FCSTD DOCUMENT  (FreeCAD 0.19R24344 (Git))
Label: MicroManipulator_Assembly_Figure2
Comment: The assembled MicroManipulator. This assembly consists of six parts. The type of arm depends on the application, the one currently shown is intended for the tethering station.
License: Creative Commons Attribution-NonCommercial-ShareAlike
LicenseURL: http://creativecommons.org/licenses/by-nc-sa/4.0/
objects: Part::FeaturePython×30, App::Link×15, App::DocumentObjectGroup×2, PartDesign::CoordinateSystem×1, App::FeaturePython×1, App::Part×1
note: 31 computed .brp shape members not serialized (recipe doc carries the construction recipe); baked Part::Feature solids carry a one-line shape summary decoded from their .brp
EXTERNAL_REF file=MicroManipulator_Rail_bottom.FCStd obj=Bottom_Mount_Edge
EXTERNAL_REF file=MicroManipulator_Rail_bottom.FCStd obj=Body
EXTERNAL_REF file=MicroManipulator_Carriage_bottom-center.FCStd obj=ScrewBottom_LCS
EXTERNAL_REF file=MicroManipulator_Rail_bottom.FCStd obj=Bottom_Cage_LCS
EXTERNAL_REF file=MicroManipulator_Carriage_bottom-center.FCStd obj=CenterSlider
EXTERNAL_REF file=MicroManipulator_Carriage_bottom-center.FCStd obj=ScrewTop_LCS
EXTERNAL_REF file=MicroManipulator_Rail_center.FCStd obj=Screw_LCS
EXTERNAL_REF file=MicroManipulator_Rail_center.FCStd obj=CenterCage
EXTERNAL_REF file=MicroManipulator_Rail_center.FCStd obj=Top_Mount_LCS
EXTERNAL_REF file=MicroManipulator_Rail_top.FCStd obj=MountPoint_LCS
EXTERNAL_REF file=MicroManipulator_Rail_top.FCStd obj=CageTop
EXTERNAL_REF file=MicroManipulator_Carriage_Hinge_top.FCStd obj=Screw_LCS
EXTERNAL_REF file=MicroManipulator_Rail_top.FCStd obj=Screw_LCS
EXTERNAL_REF file=MicroManipulator_Carriage_Hinge_top.FCStd obj=Slider
EXTERNAL_REF file=MicroManipulator_Arm_TetherStation.FCStd obj=ArmMount_LCS
EXTERNAL_REF file=MicroManipulator_Carriage_Hinge_top.FCStd obj=ArmMount_LCS
EXTERNAL_REF file=MicroManipulator_Arm_TetherStation.FCStd obj=TetherArm
EXTERNAL_REF file=MicroManipulator_Arm_tilted_Arena.FCStd obj=LCS_Hinge
EXTERNAL_REF file=MicroManipulator_Arm_tilted_Arena.FCStd obj=Body
EXTERNAL_REF file=MicroManipulator_Arm_tilted_Arena.FCStd obj=LCS_Luer
EXTERNAL_REF file=../../Miscellaneous/Luer-Tether/Luer-Tether.FCStd obj=Part
EXTERNAL_REF file=MicroManipulator_Rail_top.FCStd obj=LCS_Fasten_1
EXTERNAL_REF file=MicroManipulator_Rail_top.FCStd obj=LCS_Fasten_2
EXTERNAL_REF file=MicroManipulator_Rail_top.FCStd obj=LCS_Fasten_3
EXTERNAL_REF file=MicroManipulator_Rail_top.FCStd obj=LCS_Fasten_4
EXTERNAL_REF file=MicroManipulator_Handle.FCStd obj=LCS_Handle
EXTERNAL_REF file=MicroManipulator_Handle.FCStd obj=Body
EXTERNAL_REF file=MicroManipulator_Rail_bottom.FCStd obj=LCS_Fasten_1
EXTERNAL_REF file=MicroManipulator_Rail_bottom.FCStd obj=LCS_Fasten_2
EXTERNAL_REF file=MicroManipulator_Rail_bottom.FCStd obj=LCS_Fasten_3
EXTERNAL_REF file=MicroManipulator_Rail_bottom.FCStd obj=LCS_Fasten_4
EXTERNAL_REF file=../../Miscellaneous/Scale-Bar/Scale-Bar.FCStd obj=Scalebar

FEATURE [App::DocumentObjectGroup] Parts
FEATURE [PartDesign::CoordinateSystem] LCS_Origin
  AttacherType = Attacher::AttachEngine3D
  MapMode = 2
  Support = -> [X_Axis]
FEATURE [App::DocumentObjectGroup] Constraints
FEATURE [App::FeaturePython] Variables  # WARN: FeaturePython — macro-defined, semantics opaque (R4)
  ArmRotation = 0
  BottomMovement = 8.3
  CenterMovement = 14
  TopMovement = 5
FEATURE [App::Link] Micro_Cage_bottom
FEATURE [App::Link] Micro_Cage_bottom001
FEATURE [App::Link] Micro_Cage_bottom_Body
  AssemblyType = Asm4EE
  AttachedBy = #Bottom_Mount_Edge
  AttachedTo = Parent Assembly#LCS_Origin
  LinkPlacement = pos=(-12.7,32.4,4) rot=(0,0,-1;1.5708rad)
  LinkedObject = -> <external MicroManipulator_Rail_bottom.FCStd>#Body
  Placement = pos=(-12.7,32.4,4) rot=(0,0,-1;1.5708rad)
  expr: Placement = LCS_Origin.Placement * AttachmentOffset * MicroManipulator_Rail_bottom#Bottom_Mount_Edge.Placement ^ -1
FEATURE [App::Link] CenterSliderCombined_CenterSlider
  AssemblyType = Asm4EE
  AttachedBy = #ScrewBottom_LCS
  AttachedTo = Micro_Cage_bottom_Body#Bottom_Cage_LCS
  AttachmentOffset = pos=(0,0,8.3) rot=(0,0,1;0rad)
  LinkPlacement = pos=(-12.7,24.1,4) rot=(0,0,-1;1.5708rad)
  LinkedObject = -> <external MicroManipulator_Carriage_bottom-center.FCStd>#CenterSlider
  Placement = pos=(-12.7,24.1,4) rot=(0,0,-1;1.5708rad)
  expr: .AttachmentOffset.Base.z = Variables.BottomMovement
  expr: Placement = Micro_Cage_bottom_Body.Placement * MicroManipulator_Rail_bottom#Bottom_Cage_LCS.Placement * AttachmentOffset * MicroManipulator_Carriage_bottom_center#ScrewBottom_LCS.Placement ^ -1
FEATURE [App::Link] CenterCage
  AssemblyType = Asm4EE
  AttachedBy = #Screw_LCS
  AttachedTo = CenterSliderCombined_CenterSlider#ScrewTop_LCS
  AttachmentOffset = pos=(0,0,14) rot=(0,1,0;3.14159rad)
  LinkPlacement = pos=(-36.7,12.1,23) rot=(1,0,0;3.14159rad)
  LinkedObject = -> <external MicroManipulator_Rail_center.FCStd>#CenterCage
  Placement = pos=(-36.7,12.1,23) rot=(1,0,0;3.14159rad)
  expr: .AttachmentOffset.Base.z = Variables.CenterMovement
  expr: Placement = CenterSliderCombined_CenterSlider.Placement * MicroManipulator_Carriage_bottom_center#ScrewTop_LCS.Placement * AttachmentOffset * MicroManipulator_Rail_center#Screw_LCS.Placement ^ -1
FEATURE [App::Link] CageTop
  AssemblyType = Asm4EE
  AttachedBy = #MountPoint_LCS
  AttachedTo = CenterCage#Top_Mount_LCS
  AttachmentOffset = pos=(0,0,0) rot=(0,0,1;3.14159rad)
  LinkPlacement = pos=(-20.7,12.1,66) rot=(-3e-06,-1,2e-06;4.71239rad)
  LinkedObject = -> <external MicroManipulator_Rail_top.FCStd>#CageTop
  Placement = pos=(-20.7,12.1,66) rot=(-3e-06,-1,2e-06;4.71239rad)
  expr: Placement = CenterCage.Placement * MicroManipulator_Rail_center#Top_Mount_LCS.Placement * AttachmentOffset * MicroManipulator_Rail_top#MountPoint_LCS.Placement ^ -1
FEATURE [App::Link] SliderTop
  AssemblyType = Asm4EE
  AttachedBy = #Screw_LCS
  AttachedTo = CageTop#Screw_LCS
  AttachmentOffset = pos=(0,0,5) rot=(0,0,1;0rad)
  LinkPlacement = pos=(-20.7,12.1,63) rot=(-3e-06,-1,2e-06;4.71239rad)
  LinkedObject = -> <external MicroManipulator_Carriage_Hinge_top.FCStd>#Slider
  Placement = pos=(-20.7,12.1,63) rot=(-3e-06,-1,2e-06;4.71239rad)
  expr: .AttachmentOffset.Base.z = Variables.TopMovement
  expr: Placement = CageTop.Placement * MicroManipulator_Rail_top#Screw_LCS.Placement * AttachmentOffset * MicroManipulator_Carriage_Hinge_top#Screw_LCS.Placement ^ -1
FEATURE [App::Link] TetherArm
  AssemblyType = Asm4EE
  AttachedBy = #ArmMount_LCS
  AttachedTo = SliderTop#ArmMount_LCS
  AttachmentOffset = pos=(12,6,26) rot=(0,0,1;-0.523599rad)
  LinkPlacement = pos=(2.29989,0.0999279,76.5) rot=(0,0,1;2.61799rad)
  LinkedObject = -> <external MicroManipulator_Arm_TetherStation.FCStd>#TetherArm
  Placement = pos=(2.29989,0.0999279,76.5) rot=(0,0,1;2.61799rad)
  expr: Placement = SliderTop.Placement * MicroManipulator_Carriage_Hinge_top#ArmMount_LCS.Placement * AttachmentOffset * MicroManipulator_Arm_TetherStation#ArmMount_LCS.Placement ^ -1
FEATURE [Part::FeaturePython] Screw  # WARN: FeaturePython — macro-defined, semantics opaque (R4)
  invert = false
  offset = 0
FEATURE [Part::FeaturePython] Screw001  # WARN: FeaturePython — macro-defined, semantics opaque (R4)
  invert = false
  offset = 0
FEATURE [App::Link] MicroManipulator_Arm_tilted_Arena_Arm_tilted_Arena
  AssemblyType = Asm4EE
  AttachedBy = #LCS_Hinge
  AttachedTo = SliderTop#ArmMount_LCS
  AttachmentOffset = pos=(0,0,0) rot=(0,0,1;-0.471239rad)
  LinkPlacement = pos=(-3.70005,12.1,50.5) rot=(0,0,1;2.67035rad)
  LinkedObject = -> <external MicroManipulator_Arm_tilted_Arena.FCStd>#Body
  Placement = pos=(-3.70005,12.1,50.5) rot=(0,0,1;2.67035rad)
  expr: Placement = SliderTop.Placement * MicroManipulator_Carriage_Hinge_top#ArmMount_LCS.Placement * AttachmentOffset * MicroManipulator_Arm_tilted_Arena#LCS_Hinge.Placement ^ -1
FEATURE [App::Link] Luer_Tether_Part
  AssemblyType = Asm4EE
  AttachedBy = #LCS_Luer
  AttachedTo = MicroManipulator_Arm_tilted_Arena_Arm_tilted_Arena#LCS_Luer
  AttachmentOffset = pos=(0,0,6) rot=(0,0,1;0rad)
  LinkPlacement = pos=(52.5794,-20.6202,50.0652) rot=(0.443537,-0.72379,0.528586;1.71809rad)
  LinkedObject = -> <external ../../Miscellaneous/Luer-Tether/Luer-Tether.FCStd>#Part
  Placement = pos=(52.5794,-20.6202,50.0652) rot=(0.443537,-0.72379,0.528586;1.71809rad)
  expr: Placement = MicroManipulator_Arm_tilted_Arena_Arm_tilted_Arena.Placement * MicroManipulator_Arm_tilted_Arena#LCS_Luer.Placement * AttachmentOffset * Luer_Tether#LCS_Luer.Placement ^ -1
FEATURE [Part::FeaturePython] Washer  label="M3-Washer"  # Fasteners workbench fastener (typed FeaturePython)
  AssemblyType = Asm4EE
  AttachedBy = Origin
  AttachedTo = CageTop#Screw_LCS
  AttachmentOffset = pos=(0,0,0) rot=(1,0,0;3.14159rad)
  Placement = pos=(-15.7,12.1,68) rot=(0,0,1;1.57079rad)
  diameter = 4
  invert = false
  matchOuter = false
  offset = 0
  type = 3
  expr: Placement = CageTop.Placement * MicroManipulator_Rail_top#Screw_LCS.Placement * AttachmentOffset
FEATURE [Part::FeaturePython] Washer001  label="M3-Washer035"  # Fasteners workbench fastener (typed FeaturePython)
  AssemblyType = Asm4EE
  AttachedBy = Origin
  AttachedTo = CageTop#Screw_LCS
  AttachmentOffset = pos=(0,0,2.7) rot=(1,0,0;3.14159rad)
  Placement = pos=(-15.7,12.1,65.3) rot=(0,0,1;1.57079rad)
  diameter = 4
  invert = false
  matchOuter = false
  offset = 0
  type = 3
  expr: Placement = CageTop.Placement * MicroManipulator_Rail_top#Screw_LCS.Placement * AttachmentOffset
FEATURE [Part::FeaturePython] Screw002  label="M3x40-Screw"  # Fasteners workbench fastener (typed FeaturePython)
  AssemblyType = Asm4EE
  AttachedBy = Origin
  AttachedTo = CageTop#Screw_LCS
  AttachmentOffset = pos=(0,0,-0.5) rot=(1,0,0;3.14159rad)
  Placement = pos=(-15.7,12.1,68.5) rot=(0,0,1;1.57079rad)
  diameter = 4
  invert = false
  length = 10
  lengthCustom = 40
  matchOuter = false
  offset = 0
  thread = true
  type = 27
  expr: Placement = CageTop.Placement * MicroManipulator_Rail_top#Screw_LCS.Placement * AttachmentOffset
FEATURE [Part::FeaturePython] Nut  label="M3-Nut075"  # Fasteners workbench fastener (typed FeaturePython)
  AssemblyType = Asm4EE
  AttachedBy = Origin
  AttachedTo = CageTop#Screw_LCS
  AttachmentOffset = pos=(0,0,2.8) rot=(0,0,1;0rad)
  Placement = pos=(-15.7,12.1,65.2) rot=(0.707109,0.707105,0;3.14159rad)
  diameter = 4
  invert = false
  matchOuter = false
  offset = 0
  thread = false
  type = 7
  expr: Placement = CageTop.Placement * MicroManipulator_Rail_top#Screw_LCS.Placement * AttachmentOffset
FEATURE [Part::FeaturePython] Nut001  label="M3-Nut076"  # Fasteners workbench fastener (typed FeaturePython)
  AssemblyType = Asm4EE
  AttachedBy = Origin
  AttachedTo = SliderTop#ArmMount_LCS
  AttachmentOffset = pos=(0,0,-5) rot=(0,0,1;0rad)
  Placement = pos=(-3.70005,12.1,45.5) rot=(0,0,-1;1.5708rad)
  diameter = 4
  invert = false
  matchOuter = false
  offset = 0
  thread = false
  type = 7
  expr: Placement = SliderTop.Placement * MicroManipulator_Carriage_Hinge_top#ArmMount_LCS.Placement * AttachmentOffset
FEATURE [Part::FeaturePython] Screw003  label="M3x10-Screw"  # Fasteners workbench fastener (typed FeaturePython)
  AssemblyType = Asm4EE
  AttachedBy = Origin
  AttachedTo = SliderTop#ArmMount_LCS
  AttachmentOffset = pos=(0,0,4.4) rot=(0,0,1;0rad)
  Placement = pos=(-3.70005,12.1,54.9) rot=(0,0,-1;1.5708rad)
  diameter = 4
  invert = false
  length = 3
  lengthCustom = 10
  matchOuter = false
  offset = 0
  thread = false
  type = 27
  expr: Placement = SliderTop.Placement * MicroManipulator_Carriage_Hinge_top#ArmMount_LCS.Placement * AttachmentOffset
FEATURE [Part::FeaturePython] Screw004  label="M3x6-Screw"  # Fasteners workbench fastener (typed FeaturePython)
  AssemblyType = Asm4EE
  AttachedBy = Origin
  AttachedTo = CageTop#LCS_Fasten_1
  AttachmentOffset = pos=(0,0,0) rot=(1,0,0;3.14159rad)
  Placement = pos=(-11.7001,2.1,28) rot=(0.009203,0.012998,-0.999873;5e-06rad)
  diameter = 4
  invert = false
  length = 1
  lengthCustom = 6
  matchOuter = false
  offset = 0
  thread = false
  type = 27
  expr: Placement = CageTop.Placement * MicroManipulator_Rail_top#LCS_Fasten_1.Placement * AttachmentOffset
FEATURE [Part::FeaturePython] Screw005  label="M3x6-Screw028"  # Fasteners workbench fastener (typed FeaturePython)
  AssemblyType = Asm4EE
  AttachedBy = Origin
  AttachedTo = CageTop#LCS_Fasten_2
  AttachmentOffset = pos=(0,0,0) rot=(0,-1,0;3.14159rad)
  Placement = pos=(-21.7001,2.10005,28) rot=(0,0,1;3.14159rad)
  diameter = 4
  invert = false
  length = 1
  lengthCustom = 6
  matchOuter = false
  offset = 0
  thread = false
  type = 27
  expr: Placement = CageTop.Placement * MicroManipulator_Rail_top#LCS_Fasten_2.Placement * AttachmentOffset
FEATURE [Part::FeaturePython] Screw006  label="M3x6-Screw029"  # Fasteners workbench fastener (typed FeaturePython)
  AssemblyType = Asm4EE
  AttachedBy = Origin
  AttachedTo = CageTop#LCS_Fasten_3
  AttachmentOffset = pos=(0,0,0) rot=(1,0,0;3.14159rad)
  Placement = pos=(-11.7,22.1,28) rot=(0.009203,0.012998,-0.999873;5e-06rad)
  diameter = 4
  invert = false
  length = 1
  lengthCustom = 6
  matchOuter = false
  offset = 0
  thread = false
  type = 27
  expr: Placement = CageTop.Placement * MicroManipulator_Rail_top#LCS_Fasten_3.Placement * AttachmentOffset
FEATURE [Part::FeaturePython] Screw007  label="M3x6-Screw030"  # Fasteners workbench fastener (typed FeaturePython)
  AssemblyType = Asm4EE
  AttachedBy = Origin
  AttachedTo = CageTop#LCS_Fasten_4
  AttachmentOffset = pos=(0,0,0) rot=(1,0,0;3.14159rad)
  Placement = pos=(-21.7,22.1,28) rot=(0.009203,0.012998,-0.999873;5e-06rad)
  diameter = 4
  invert = false
  length = 1
  lengthCustom = 6
  matchOuter = false
  offset = 0
  thread = false
  type = 27
  expr: Placement = CageTop.Placement * MicroManipulator_Rail_top#LCS_Fasten_4.Placement * AttachmentOffset
FEATURE [Part::FeaturePython] Nut002  label="M3-Nut"  # Fasteners workbench fastener (typed FeaturePython)
  AssemblyType = Asm4EE
  AttachedBy = Origin
  AttachedTo = SliderTop#Screw_LCS
  AttachmentOffset = pos=(0,0,4.5) rot=(0,0,-1;1.5708rad)
  Placement = pos=(-15.7,12.1,58.5) rot=(2e-06,1,0;3.14159rad)
  diameter = 4
  invert = false
  matchOuter = false
  offset = 0
  thread = false
  type = 7
  expr: Placement = SliderTop.Placement * MicroManipulator_Carriage_Hinge_top#Screw_LCS.Placement * AttachmentOffset
FEATURE [Part::FeaturePython] Nut003  label="M3-Nut077"  # Fasteners workbench fastener (typed FeaturePython)
  AssemblyType = Asm4EE
  AttachedBy = Origin
  AttachedTo = CageTop#LCS_Fasten_1
  AttachmentOffset = pos=(0,0,4) rot=(0,0,-1;3.14159rad)
  Placement = pos=(-11.7001,2.1,24) rot=(3e-06,1,0;3.14159rad)
  diameter = 4
  invert = false
  matchOuter = false
  offset = 0
  thread = false
  type = 7
  expr: Placement = CageTop.Placement * MicroManipulator_Rail_top#LCS_Fasten_1.Placement * AttachmentOffset
FEATURE [Part::FeaturePython] Nut004  label="M3-Nut078"  # Fasteners workbench fastener (typed FeaturePython)
  AssemblyType = Asm4EE
  AttachedBy = Origin
  AttachedTo = CageTop#LCS_Fasten_2
  AttachmentOffset = pos=(0,0,4) rot=(0,0,1;0rad)
  Placement = pos=(-21.7001,2.10005,24) rot=(1,-3e-06,0;3.14159rad)
  diameter = 4
  invert = false
  matchOuter = false
  offset = 0
  thread = false
  type = 7
  expr: Placement = CageTop.Placement * MicroManipulator_Rail_top#LCS_Fasten_2.Placement * AttachmentOffset
FEATURE [Part::FeaturePython] Nut005  label="M3-Nut079"  # Fasteners workbench fastener (typed FeaturePython)
  AssemblyType = Asm4EE
  AttachedBy = Origin
  AttachedTo = CageTop#LCS_Fasten_3
  AttachmentOffset = pos=(0,0,4) rot=(0,0,1;0rad)
  Placement = pos=(-11.7,22.1,24) rot=(1,-3e-06,0;3.14159rad)
  diameter = 4
  invert = false
  matchOuter = false
  offset = 0
  thread = false
  type = 7
  expr: Placement = CageTop.Placement * MicroManipulator_Rail_top#LCS_Fasten_3.Placement * AttachmentOffset
FEATURE [Part::FeaturePython] Nut006  label="M3-Nut080"  # Fasteners workbench fastener (typed FeaturePython)
  AssemblyType = Asm4EE
  AttachedBy = Origin
  AttachedTo = CageTop#LCS_Fasten_4
  AttachmentOffset = pos=(0,0,4) rot=(0,0,1;0rad)
  Placement = pos=(-21.7,22.1,24) rot=(1,-3e-06,0;3.14159rad)
  diameter = 4
  invert = false
  matchOuter = false
  offset = 0
  thread = false
  type = 7
  expr: Placement = CageTop.Placement * MicroManipulator_Rail_top#LCS_Fasten_4.Placement * AttachmentOffset
FEATURE [Part::FeaturePython] Screw008  label="M3x40-Screw007"  # Fasteners workbench fastener (typed FeaturePython)
  AssemblyType = Asm4EE
  AttachedBy = Origin
  AttachedTo = CenterCage#Screw_LCS
  AttachmentOffset = pos=(0,0,-0.7) rot=(1,0,0;3.14159rad)
  Placement = pos=(-39.4,12.1,18) rot=(0.57735,-0.57735,-0.57735;2.0944rad)
  diameter = 4
  invert = false
  length = 10
  lengthCustom = 40
  matchOuter = false
  offset = 0
  thread = true
  type = 27
  expr: Placement = CenterCage.Placement * MicroManipulator_Rail_center#Screw_LCS.Placement * AttachmentOffset
FEATURE [Part::FeaturePython] Washer002  label="M3-Washer033"  # Fasteners workbench fastener (typed FeaturePython)
  AssemblyType = Asm4EE
  AttachedBy = Origin
  AttachedTo = CenterCage#Screw_LCS
  AttachmentOffset = pos=(0,0,0) rot=(1,0,0;3.14159rad)
  Placement = pos=(-38.7,12.1,18) rot=(0.57735,-0.57735,-0.57735;2.0944rad)
  diameter = 4
  invert = false
  matchOuter = false
  offset = 0
  type = 3
  expr: Placement = CenterCage.Placement * MicroManipulator_Rail_center#Screw_LCS.Placement * AttachmentOffset
FEATURE [Part::FeaturePython] Washer003  label="M3-Washer034"  # Fasteners workbench fastener (typed FeaturePython)
  AssemblyType = Asm4EE
  AttachedBy = Origin
  AttachedTo = CenterCage#Screw_LCS
  AttachmentOffset = pos=(0,0,2) rot=(0,0,1;0rad)
  Placement = pos=(-36.7,12.1,18) rot=(0.57735,-0.57735,0.57735;4.18879rad)
  diameter = 4
  invert = false
  matchOuter = false
  offset = 0
  type = 3
  expr: Placement = CenterCage.Placement * MicroManipulator_Rail_center#Screw_LCS.Placement * AttachmentOffset
FEATURE [Part::FeaturePython] Nut007  label="M3-Nut081"  # Fasteners workbench fastener (typed FeaturePython)
  AssemblyType = Asm4EE
  AttachedBy = Origin
  AttachedTo = CenterCage#Screw_LCS
  AttachmentOffset = pos=(0,0,2.8) rot=(0,0,1;0rad)
  Placement = pos=(-35.9,12.1,18) rot=(0.57735,-0.57735,0.57735;4.18879rad)
  diameter = 4
  invert = false
  matchOuter = false
  offset = 0
  thread = false
  type = 7
  expr: Placement = CenterCage.Placement * MicroManipulator_Rail_center#Screw_LCS.Placement * AttachmentOffset
FEATURE [Part::FeaturePython] Screw009  label="M3x40-Screw006"  # Fasteners workbench fastener (typed FeaturePython)
  AssemblyType = Asm4EE
  AttachedBy = Origin
  AttachedTo = Micro_Cage_bottom_Body#Bottom_Cage_LCS
  AttachmentOffset = pos=(0,0,-0.7) rot=(1,0,0;3.14159rad)
  Placement = pos=(-12.7,33.1,9) rot=(-1,0,0;1.5708rad)
  diameter = 4
  invert = false
  length = 10
  lengthCustom = 40
  matchOuter = false
  offset = 0
  thread = true
  type = 27
  expr: Placement = Micro_Cage_bottom_Body.Placement * MicroManipulator_Rail_bottom#Bottom_Cage_LCS.Placement * AttachmentOffset
FEATURE [Part::FeaturePython] Washer004  label="M3-Washer028"  # Fasteners workbench fastener (typed FeaturePython)
  AssemblyType = Asm4EE
  AttachedBy = Origin
  AttachedTo = Micro_Cage_bottom_Body#Bottom_Cage_LCS
  AttachmentOffset = pos=(0,0,0) rot=(1,0,0;3.14159rad)
  Placement = pos=(-12.7,32.4,9) rot=(-1,0,0;1.5708rad)
  diameter = 4
  invert = false
  matchOuter = false
  offset = 0
  type = 3
  expr: Placement = Micro_Cage_bottom_Body.Placement * MicroManipulator_Rail_bottom#Bottom_Cage_LCS.Placement * AttachmentOffset
FEATURE [Part::FeaturePython] Washer005  label="M3-Washer029"  # Fasteners workbench fastener (typed FeaturePython)
  AssemblyType = Asm4EE
  AttachedBy = Origin
  AttachedTo = Micro_Cage_bottom_Body#Bottom_Cage_LCS
  AttachmentOffset = pos=(0,0,2) rot=(0,0,1;0rad)
  Placement = pos=(-12.7,30.4,9) rot=(1,0,0;1.5708rad)
  diameter = 4
  invert = false
  matchOuter = false
  offset = 0
  type = 3
  expr: Placement = Micro_Cage_bottom_Body.Placement * MicroManipulator_Rail_bottom#Bottom_Cage_LCS.Placement * AttachmentOffset
FEATURE [Part::FeaturePython] Nut008  label="M3-Nut064"  # Fasteners workbench fastener (typed FeaturePython)
  AssemblyType = Asm4EE
  AttachedBy = Origin
  AttachedTo = Micro_Cage_bottom_Body#Bottom_Cage_LCS
  AttachmentOffset = pos=(0,0,2.7) rot=(0,0,1;0rad)
  Placement = pos=(-12.7,29.7,9) rot=(1,0,0;1.5708rad)
  diameter = 4
  invert = false
  matchOuter = false
  offset = 0
  thread = false
  type = 7
  expr: Placement = Micro_Cage_bottom_Body.Placement * MicroManipulator_Rail_bottom#Bottom_Cage_LCS.Placement * AttachmentOffset
FEATURE [Part::FeaturePython] Nut009  label="M3-Nut082"  # Fasteners workbench fastener (typed FeaturePython)
  AssemblyType = Asm4EE
  AttachedBy = Origin
  AttachedTo = CageTop#Screw_LCS
  AttachmentOffset = pos=(0,0,22) rot=(0,0,1;0rad)
  Placement = pos=(-15.7,12.1,46) rot=(0.707109,0.707105,0;3.14159rad)
  diameter = 4
  invert = false
  matchOuter = false
  offset = 0
  thread = false
  type = 7
  expr: Placement = CageTop.Placement * MicroManipulator_Rail_top#Screw_LCS.Placement * AttachmentOffset
FEATURE [App::Link] MicroManipulator_Handle_Handle
  AssemblyType = Asm4EE
  AttachedBy = #LCS_Handle
  AttachedTo = Micro_Cage_bottom_Body#Bottom_Cage_LCS
  AttachmentOffset = pos=(0,0,-1) rot=(1,0,0;3.14159rad)
  LinkPlacement = pos=(-12.7,33.4,9) rot=(0.935113,0.250563,0.250563;4.64535rad)
  LinkedObject = -> <external MicroManipulator_Handle.FCStd>#Body
  Placement = pos=(-12.7,33.4,9) rot=(0.935113,0.250563,0.250563;4.64535rad)
  expr: Placement = Micro_Cage_bottom_Body.Placement * MicroManipulator_Rail_bottom#Bottom_Cage_LCS.Placement * AttachmentOffset * MicroManipulator_Handle#LCS_Handle.Placement ^ -1
FEATURE [App::Link] MicroManipulator_Handle_Handle001
  AssemblyType = Asm4EE
  AttachedBy = #LCS_Handle
  AttachedTo = CenterCage#Screw_LCS
  AttachmentOffset = pos=(0,0,-1) rot=(1,0,0;3.14159rad)
  LinkPlacement = pos=(-39.7,12.1,18) rot=(-0.654654,0.377964,0.654654;3.86433rad)
  LinkedObject = -> <external MicroManipulator_Handle.FCStd>#Body
  Placement = pos=(-39.7,12.1,18) rot=(-0.654654,0.377964,0.654654;3.86433rad)
  expr: Placement = CenterCage.Placement * MicroManipulator_Rail_center#Screw_LCS.Placement * AttachmentOffset * MicroManipulator_Handle#LCS_Handle.Placement ^ -1
FEATURE [App::Link] MicroManipulator_Handle_Handle002
  AssemblyType = Asm4EE
  AttachedBy = #LCS_Handle
  AttachedTo = CageTop#Screw_LCS
  AttachmentOffset = pos=(0,0,-1) rot=(1,0,0;3.14159rad)
  LinkPlacement = pos=(-15.7,12.1,69) rot=(0,0,1;1.04719rad)
  LinkedObject = -> <external MicroManipulator_Handle.FCStd>#Body
  Placement = pos=(-15.7,12.1,69) rot=(0,0,1;1.04719rad)
  expr: Placement = CageTop.Placement * MicroManipulator_Rail_top#Screw_LCS.Placement * AttachmentOffset * MicroManipulator_Handle#LCS_Handle.Placement ^ -1
FEATURE [Part::FeaturePython] Screw010  label="M5x8-Screw"  # Fasteners workbench fastener (typed FeaturePython)
  AssemblyType = Asm4EE
  AttachedBy = Origin
  AttachedTo = Micro_Cage_bottom_Body#LCS_Fasten_1
  Placement = pos=(0.257161,1.4e-14,3) rot=(0,0,1;0rad)
  diameter = 7
  invert = false
  length = 0
  lengthCustom = 8
  matchOuter = false
  offset = 0
  thread = false
  type = 27
  expr: Placement = Micro_Cage_bottom_Body.Placement * MicroManipulator_Rail_bottom#LCS_Fasten_1.Placement * AttachmentOffset
FEATURE [Part::FeaturePython] Screw011  label="M5x8-Screw004"  # Fasteners workbench fastener (typed FeaturePython)
  AssemblyType = Asm4EE
  AttachedBy = Origin
  AttachedTo = Micro_Cage_bottom_Body#LCS_Fasten_2
  Placement = pos=(0.257161,25.4,3) rot=(0,0,1;0rad)
  diameter = 7
  invert = false
  length = 0
  lengthCustom = 8
  matchOuter = false
  offset = 0
  thread = false
  type = 27
  expr: Placement = Micro_Cage_bottom_Body.Placement * MicroManipulator_Rail_bottom#LCS_Fasten_2.Placement * AttachmentOffset
FEATURE [Part::FeaturePython] Screw012  label="M5x8-Screw005"  # Fasteners workbench fastener (typed FeaturePython)
  AssemblyType = Asm4EE
  AttachedBy = Origin
  AttachedTo = Micro_Cage_bottom_Body#LCS_Fasten_3
  Placement = pos=(-25.6572,25.4,3) rot=(0,0,1;0rad)
  diameter = 7
  invert = false
  length = 0
  lengthCustom = 8
  matchOuter = false
  offset = 0
  thread = false
  type = 27
  expr: Placement = Micro_Cage_bottom_Body.Placement * MicroManipulator_Rail_bottom#LCS_Fasten_3.Placement * AttachmentOffset
FEATURE [Part::FeaturePython] Screw013  label="M5x8-Screw006"  # Fasteners workbench fastener (typed FeaturePython)
  AssemblyType = Asm4EE
  AttachedBy = Origin
  AttachedTo = Micro_Cage_bottom_Body#LCS_Fasten_4
  Placement = pos=(-25.6572,7e-15,3) rot=(0,0,1;0rad)
  diameter = 7
  invert = false
  length = 0
  lengthCustom = 8
  matchOuter = false
  offset = 0
  thread = false
  type = 27
  expr: Placement = Micro_Cage_bottom_Body.Placement * MicroManipulator_Rail_bottom#LCS_Fasten_4.Placement * AttachmentOffset
FEATURE [App::Link] MicroManipulator_Arm_TetherStation_Arm_TetherStation
  AssemblyType = Asm4EE
  AttachedBy = #ArmMount_LCS
  AttachedTo = SliderTop#ArmMount_LCS
  AttachmentOffset = pos=(17,0,0) rot=(0,0,1;-0.785398rad)
  LinkPlacement = pos=(-3.70013,-4.90004,50.5) rot=(0,0,1;2.35619rad)
  LinkedObject = -> <external MicroManipulator_Arm_TetherStation.FCStd>#TetherArm
  Placement = pos=(-3.70013,-4.90004,50.5) rot=(0,0,1;2.35619rad)
  expr: Placement = SliderTop.Placement * MicroManipulator_Carriage_Hinge_top#ArmMount_LCS.Placement * AttachmentOffset * MicroManipulator_Arm_TetherStation#ArmMount_LCS.Placement ^ -1
FEATURE [App::Link] Scale_Bar_Scalebar
  AssemblyType = Asm4EE
  AttachedBy = #LCS_0
  AttachedTo = Parent Assembly#LCS_Origin
  AttachmentOffset = pos=(17,-35,0) rot=(0,0.707107,0.707107;3.14159rad)
  LinkPlacement = pos=(17,-35,0) rot=(0,0.707107,0.707107;3.14159rad)
  LinkedObject = -> <external ../../Miscellaneous/Scale-Bar/Scale-Bar.FCStd>#Scalebar
  Placement = pos=(17,-35,0) rot=(0,0.707107,0.707107;3.14159rad)
  expr: Placement = LCS_Origin.Placement * AttachmentOffset * Scale_Bar#LCS_0.Placement ^ -1
FEATURE [App::Part] Model  label="Assembled Manipulator"
  Configuration = 0
  Group = -> [LCS_Origin,Constraints,Variables,Micro_Cage_bottom,Micro_Cage_bottom001,Micro_Cage_bottom_Body,CenterSliderCombined_CenterSlider,CenterCage,CageTop,SliderTop,TetherArm,MicroManipulator_Arm_tilted_Arena_Arm_tilted_Arena,Luer_Tether_Part,Washer,Screw002,Nut002,Nut,Nut001,Screw003,Screw004,Screw005,Screw006,Screw007,Nut003,Nut004,Nut005,Nut006,Screw008,Washer002,Washer003,Nut007,Washer001,Screw009,+13 more]
  Origin = -> Origin
  Type = Assembly4 Model

RESOLVED EXTERNAL PARTS (link-assembly join: the EXTERNAL_REF files above that resolve inside this repo's crawl, each included once):
---- part ../../Miscellaneous/Luer-Tether/Luer-Tether.FCStd = doc fcstd_4625ed215820 ----
FCSTD DOCUMENT  (FreeCAD 0.19R24344 (Git))
Label: Luer-Tether
License: All rights reserved
LicenseURL: http://en.wikipedia.org/wiki/All_rights_reserved
objects: Part::Feature×2, PartDesign::CoordinateSystem×2, Sketcher::SketchObject×1, PartDesign::Pad×1, PartDesign::Body×1, Part::Compound2×1, Part::FeaturePython×1, App::Part×1
note: 9 computed .brp shape members not serialized (recipe doc carries the construction recipe); baked Part::Feature solids carry a one-line shape summary decoded from their .brp

FEATURE [Part::Feature] Solid
  shape: bbox 18.46 x 7.75 x 8.149 mm, 114 faces (baked)
FEATURE [Sketcher::SketchObject] Sketch
  FullyConstrained = true
  MapMode = 5
  Placement = pos=(0,0,0) rot=(0.57735,0.57735,0.57735;2.0944rad)
  Support = -> [YZ_Plane]
  sketch-geometry (2):
    g0: Circle CenterX=0 CenterY=0 CenterZ=0 NormalX=0 NormalY=0 NormalZ=1 AngleXU=0 Radius=0.1175
    g1: Circle CenterX=0 CenterY=0 CenterZ=0 NormalX=0 NormalY=0 NormalZ=1 AngleXU=0 Radius=0.054
  constraints (4):
    c: Diameter(g0) = 0.235
    c: Diameter(g1) = 0.108
    c: Coincident(g0,g-1)
    c: Coincident(g1,g0)
FEATURE [PartDesign::Pad] Pad
  Direction = (1,1,1)
  Length = 20.4
  Length2 = 100
  Placement = pos=(0,0,0) rot=(0.57735,0.57735,0.57735;2.0944rad)
  Profile = -> Sketch
  Reversed = true
  Type = 0
FEATURE [PartDesign::Body] Body
  Group = -> [Sketch,Pad]
  Origin = -> Origin
  Tip = -> Pad
FEATURE [PartDesign::CoordinateSystem] LCS_0
  AttacherType = Attacher::AttachEngine3D
  MapMode = 2
  Support = -> [X_Axis001]
FEATURE [Part::Feature] Solid001
  shape: bbox 30.9 x 0.91 x 0.91 mm, 6 faces (baked)
FEATURE [Part::Compound2] Compound  label="Syringe Tip"
  Links = -> [Solid,Solid001]
FEATURE [Part::FeaturePython] Compound_child0  label="Luer"  # WARN: FeaturePython — macro-defined, semantics opaque (R4)
  Base = -> Compound
  FilterType = 1
  Invert = false
  OverrideMaxVal = 0
  WindowFrom = 80
  WindowTo = 100
  items = 0
FEATURE [PartDesign::CoordinateSystem] LCS_Luer
  AttacherType = Attacher::AttachEngine3D
  MapMode = 45
  Placement = pos=(17.75,-9e-16,1e-16) rot=(0.57735,0.57735,0.57735;2.0944rad)
  Support = -> [Compound_child0]
FEATURE [App::Part] Part
  Group = -> [LCS_0,Solid,Solid001,Compound,Body,Compound_child0,LCS_Luer]
  Origin = -> Origin001
---- part ../../Miscellaneous/Scale-Bar/Scale-Bar.FCStd = doc fcstd_313a3d742b27 ----
FCSTD DOCUMENT  (FreeCAD 0.19R24344 (Git))
Label: Scale Bar
License: Creative Commons Attribution-NonCommercial-ShareAlike
LicenseURL: http://creativecommons.org/licenses/by-nc-sa/4.0/
objects: Part::Box×15, Part::Part2DObjectPython×2, PartDesign::CoordinateSystem×1, App::Part×1
note: 18 computed .brp shape members not serialized (recipe doc carries the construction recipe); baked Part::Feature solids carry a one-line shape summary decoded from their .brp

FEATURE [Part::Box] Box  label="Cube"
  AttacherType = Attacher::AttachEngine3D
  Height = 1
  Length = 10
  Placement = pos=(-10,0,0) rot=(0,0,1;0rad)
  Width = 1
FEATURE [Part::Box] Box001  label="Cube001"
  AttacherType = Attacher::AttachEngine3D
  Height = 1
  Length = 1
  Placement = pos=(-16,0,0) rot=(0,0,1;0rad)
  Width = 1
FEATURE [Part::Box] Box002  label="Cube002"
  AttacherType = Attacher::AttachEngine3D
  Height = 1
  Length = 1
  Placement = pos=(-18,0,0) rot=(0,0,1;0rad)
  Width = 1
FEATURE [Part::Box] Box003  label="Cube003"
  AttacherType = Attacher::AttachEngine3D
  Height = 1
  Length = 1
  Placement = pos=(-20,0,0) rot=(0,0,1;0rad)
  Width = 1
FEATURE [PartDesign::CoordinateSystem] LCS_0
  AttacherType = Attacher::AttachEngine3D
  MapMode = 2
  Support = -> [X_Axis]
FEATURE [Part::Box] Box004  label="Cube004"
  AttacherType = Attacher::AttachEngine3D
  Height = 1
  Length = 10
  Placement = pos=(-1,10,0) rot=(0,0,-1;1.5708rad)
  Width = 1
FEATURE [Part::Box] Box005  label="Cube005"
  AttacherType = Attacher::AttachEngine3D
  Height = 1
  Length = 1
  Placement = pos=(-1,16,0) rot=(0,0,-1;1.5708rad)
  Width = 1
FEATURE [Part::Box] Box006  label="Cube006"
  AttacherType = Attacher::AttachEngine3D
  Height = 1
  Length = 1
  Placement = pos=(-1,18,0) rot=(0,0,-1;1.5708rad)
  Width = 1
FEATURE [Part::Box] Box007  label="Cube007"
  AttacherType = Attacher::AttachEngine3D
  Height = 1
  Length = 1
  Placement = pos=(-1,20,0) rot=(0,0,-1;1.5708rad)
  Width = 1
FEATURE [Part::Box] Box010  label="Cube010"
  AttacherType = Attacher::AttachEngine3D
  Height = 1
  Length = 1
  Placement = pos=(-1,0,18) rot=(0,1,0;1.5708rad)
  Width = 1
FEATURE [Part::Box] Box008  label="Cube008"
  AttacherType = Attacher::AttachEngine3D
  Height = 1
  Length = 10
  Placement = pos=(-1,0,10) rot=(0,1,0;1.5708rad)
  Width = 1
FEATURE [Part::Box] Box009  label="Cube009"
  AttacherType = Attacher::AttachEngine3D
  Height = 1
  Length = 1
  Placement = pos=(-1,0,16) rot=(0,1,0;1.5708rad)
  Width = 1
FEATURE [Part::Box] Box011  label="Cube011"
  AttacherType = Attacher::AttachEngine3D
  Height = 1
  Length = 1
  Placement = pos=(-1,0,20) rot=(0,1,0;1.5708rad)
  Width = 1
FEATURE [Part::Box] Box012  label="Cube012"
  AttacherType = Attacher::AttachEngine3D
  Height = 19.9
  Length = 0.9
  Placement = pos=(-0.95,0.05,0) rot=(0,0,1;0rad)
  Width = 0.9
FEATURE [Part::Box] Box013  label="Cube013"
  AttacherType = Attacher::AttachEngine3D
  Height = 0.9
  Length = 19.9
  Placement = pos=(-19.95,0.05,0.05) rot=(0,0,1;0rad)
  Width = 0.9
FEATURE [Part::Box] Box014  label="Cube014"
  AttacherType = Attacher::AttachEngine3D
  Height = 0.9
  Length = 0.9
  Placement = pos=(-0.95,0.05,0.05) rot=(0,0,1;0rad)
  Width = 19.9
FEATURE [Part::Part2DObjectPython] ShapeString  label="X-Label"  # Draft 2D object (typed FeaturePython)
  FontFile = <userpath>/prj/2019_Janelia_Component-Design/Extra/Scale Bar/DejaVuSans.ttf
  Placement = pos=(-18.94,2,0) rot=(0,0,1;0rad)
  Size = 4
  String = 20mm
  Tracking = 0
FEATURE [Part::Part2DObjectPython] ShapeString001  label="Y-Label"  # Draft 2D object (typed FeaturePython)
  FontFile = <userpath>/prj/2019_Janelia_Component-Design/Extra/Scale Bar/DejaVuSans.ttf
  Placement = pos=(0,2,2) rot=(0,1,0;36.1283rad)
  Size = 4
  String = 20mm
  Tracking = 0
FEATURE [App::Part] Scalebar
  Group = -> [LCS_0,Box,Box001,Box002,Box003,Box004,Box005,Box006,Box007,Box008,Box009,Box010,Box011,Box012,Box013,Box014,ShapeString,ShapeString001]
  Origin = -> Origin
---- part MicroManipulator_Arm_TetherStation.FCStd = doc fcstd_4e07fe916bf2 ----
FCSTD DOCUMENT  (FreeCAD 0.19R24344 (Git))
Label: MicroManipulator_Arm_TetherStation
Comment: Arm for the MicroManipulator. The friction mount point for the Luer lock has the same angle as the holder of the peltier element. This angle is for installing the manipualtor on the left side of the p... (+15 chars)
License: Creative Commons Attribution-NonCommercial-ShareAlike
LicenseURL: http://creativecommons.org/licenses/by-nc-sa/4.0/
objects: Sketcher::SketchObject×4, PartDesign::CoordinateSystem×2, PartDesign::Pad×1, PartDesign::AdditivePipe×1, PartDesign::Line×1, PartDesign::Revolution×1, PartDesign::Body×1, App::Part×1
note: 14 computed .brp shape members not serialized (recipe doc carries the construction recipe); baked Part::Feature solids carry a one-line shape summary decoded from their .brp

FEATURE [Sketcher::SketchObject] Sketch
  FullyConstrained = true
  MapMode = 5
  Support = -> [XY_Plane]
  sketch-geometry (5):
    g0: Circle CenterX=0 CenterY=0 CenterZ=0 NormalX=0 NormalY=0 NormalZ=1 AngleXU=0 Radius=1.55
    g1: LineSegment StartX=1.23043e-11 StartY=2.5 StartZ=0 EndX=-7 EndY=2.5 EndZ=0
    g2: LineSegment StartX=-7 StartY=2.5 StartZ=0 EndX=-7 EndY=-2.5 EndZ=0
    g3: LineSegment StartX=1.23043e-11 StartY=-2.5 StartZ=0 EndX=-7 EndY=-2.5 EndZ=0
    g4: ArcOfCircle CenterX=0 CenterY=0 CenterZ=0 NormalX=0 NormalY=0 NormalZ=1 AngleXU=0 Radius=2.5 StartAngle=4.71239 EndAngle=7.85398
  constraints (14):
    c: Diameter(g0) = 3.1
    c: Horizontal(g1)
    c: Coincident(g2,g1)
    c: Vertical(g2)
    c: Coincident(g3,g2)
    c: Horizontal(g3)
    c: Coincident(g4,g1)
    c: Coincident(g4,g3)
    c: Angle(g4) = 3.14159
    c: Distance(g3,g1) = 5
    c: Vertical(g3,g1)
    c: Coincident(g4,g0)
    c: Coincident(g0,g-1)
    c: Distance(g3) = 7
FEATURE [PartDesign::Pad] Pad
  Direction = (1,1,1)
  Length = 2
  Length2 = 100
  Profile = -> Sketch
  Type = 0
FEATURE [Sketcher::SketchObject] Sketch001
  ExternalGeometry = -> [Pad]
  FullyConstrained = true
  MapMode = 5
  Placement = pos=(0,0,0) rot=(1,0,0;1.5708rad)
  Support = -> [XZ_Plane]
  sketch-geometry (2):
    g0: ArcOfCircle CenterX=-27 CenterY=-1.2e-15 CenterZ=0 NormalX=0 NormalY=0 NormalZ=1 AngleXU=0 Radius=20 StartAngle=0 EndAngle=1.5708
    g1: LineSegment StartX=-27 StartY=20 StartZ=0 EndX=-85 EndY=20 EndZ=0
  constraints (6):
    c: Coincident(g0,g-3)
    c: Horizontal(g1)
    c: DistanceX(g1,g-1) = 85
    c: DistanceY(g-1,g1) = 20
    c: Tangent(g1,g0) = -1.5708
    c: Angle(g0) = 1.5708
FEATURE [Sketcher::SketchObject] Sketch002
  ExternalGeometry = -> [Sketch001]
  FullyConstrained = true
  MapMode = 5
  Support = -> [XY_Plane]
  sketch-geometry (7):
    g0: LineSegment StartX=-8.44338 StartY=-2.5 StartZ=0 EndX=-5.55662 EndY=-2.5 EndZ=0
    g1: LineSegment StartX=-5.55662 StartY=-2.5 StartZ=0 EndX=-4.11325 EndY=4e-16 EndZ=0
    g2: LineSegment StartX=-4.11325 StartY=4e-16 StartZ=0 EndX=-5.55662 EndY=2.5 EndZ=0
    g3: LineSegment StartX=-5.55662 StartY=2.5 StartZ=0 EndX=-8.44338 EndY=2.5 EndZ=0
    g4: LineSegment StartX=-8.44338 StartY=2.5 StartZ=0 EndX=-9.88675 EndY=0 EndZ=0
    g5: LineSegment StartX=-9.88675 StartY=0 StartZ=0 EndX=-8.44338 EndY=-2.5 EndZ=0
    g6: Circle CenterX=-7 CenterY=0 CenterZ=0 NormalX=0 NormalY=0 NormalZ=1 AngleXU=0 Radius=2.88675
  constraints (16):
    c: Coincident(g0,g1)
    c: Coincident(g1,g2)
    c: Coincident(g2,g3)
    c: Coincident(g3,g4)
    c: Coincident(g4,g5)
    c: Coincident(g5,g0)
    c: Equal(g0, g1-g5) x5
    c: PointOnObject(g0,g6)
    c: PointOnObject(g1,g6)
    c: PointOnObject(g2,g6)
    c: PointOnObject(g3,g6)
    c: PointOnObject(g4,g6)
    c: PointOnObject(g5,g6)
    c: DistanceY(g0,g3) = 5
    c: Horizontal(g0)
    c: Coincident(g6,g-3)
FEATURE [PartDesign::AdditivePipe] AdditivePipe
  AuxilleryCurvelinear = true
  AuxillerySpineTangent = false
  BaseFeature = -> Pad
  Binormal = (0,0,0)
  Mode = 2
  Profile = -> Sketch002
  Spine = -> Sketch001
  SpineTangent = false
  Transformation = 0
  Transition = 0
FEATURE [Sketcher::SketchObject] Sketch003
  ExternalGeometry = -> [Sketch001]
  FullyConstrained = true
  MapMode = 5
  Placement = pos=(-85,0,0) rot=(0.57735,-0.57735,-0.57735;2.0944rad)
  Support = -> [AdditivePipe]
  sketch-geometry (4):
    g0: LineSegment StartX=4.4e-15 StartY=20 StartZ=0 EndX=4.10424 EndY=8.72369 EndZ=0
    g1: LineSegment StartX=4.4e-15 StartY=20 StartZ=0 EndX=2.48467 EndY=20 EndZ=0
    g2: LineSegment StartX=2.48467 StartY=20 StartZ=0 EndX=5.98363 EndY=9.40773 EndZ=0
    g3: LineSegment StartX=5.98363 StartY=9.40773 StartZ=0 EndX=4.10424 EndY=8.72369 EndZ=0
  constraints (11):
    c: Coincident(g1,g0)
    c: Horizontal(g1)
    c: Coincident(g2,g1)
    c: Coincident(g3,g2)
    c: Distance(g0) = 12
    c: Distance(g3) = 2
    c: Coincident(g0,g-3)
    c: Coincident(g3,g0)
    c: Angle(g-2,g0) = 0.349066
    c: Angle(g2,g0) = 0.0300197
    c: Perpendicular(g0,g3)
FEATURE [PartDesign::Line] DatumLine
  AttacherType = Attacher::AttachEngineLine
  Length = 20
  MapMode = 29
  Placement = pos=(-85,-6.42788,2.33956) rot=(1,0,0;2.79253rad)
  ResizeMode = 0
  Support = -> [Sketch003]
FEATURE [PartDesign::Revolution] Revolution
  Angle = 360
  Axis = (0,-0.34202,-0.939693)
  Base = (-85,-6.42788,2.33956)
  BaseFeature = -> AdditivePipe
  Profile = -> Sketch003
  ReferenceAxis = -> DatumLine
  Reversed = true
FEATURE [PartDesign::Body] Body
  Group = -> [Sketch,Pad,Sketch001,Sketch002,AdditivePipe,Sketch003,Revolution,DatumLine]
  Origin = -> Origin
  Tip = -> Revolution
FEATURE [PartDesign::CoordinateSystem] LCS_0
  AttacherType = Attacher::AttachEngine3D
  MapMode = 2
  Support = -> [X_Axis001]
FEATURE [PartDesign::CoordinateSystem] ArmMount_LCS
  AttacherType = Attacher::AttachEngine3D
  AttachmentOffset = pos=(0,0,0) rot=(0,0,1;1.5708rad)
  MapMode = 45
  Placement = pos=(7.3e-15,0,0) rot=(0,0,1;1.5708rad)
  Support = -> [Revolution]
FEATURE [App::Part] TetherArm  label="Arm_TetherStation"
  Group = -> [LCS_0,Body,ArmMount_LCS]
  Origin = -> Origin001
---- part MicroManipulator_Arm_tilted_Arena.FCStd = doc fcstd_c2bd71447b71 ----
FCSTD DOCUMENT  (FreeCAD 0.19R24344 (Git))
Label: MicroManipulator_Arm_tilted_Arena
Comment: Arm for the MicroManipulator. The friction mount point for the Luer lock item tilted so that the animal is not exactly on top of the treadmill but instead is always in a 10° upward angle.
License: Creative Commons Attribution-NonCommercial-ShareAlike
LicenseURL: http://creativecommons.org/licenses/by-nc-sa/4.0/
objects: Sketcher::SketchObject×4, PartDesign::CoordinateSystem×2, PartDesign::Pad×1, PartDesign::AdditivePipe×1, PartDesign::Plane×1, PartDesign::Revolution×1, PartDesign::Body×1
note: 14 computed .brp shape members not serialized (recipe doc carries the construction recipe); baked Part::Feature solids carry a one-line shape summary decoded from their .brp

FEATURE [Sketcher::SketchObject] Sketch
  FullyConstrained = true
  MapMode = 5
  Support = -> [XY_Plane]
  sketch-geometry (5):
    g0: Circle CenterX=0 CenterY=0 CenterZ=0 NormalX=0 NormalY=0 NormalZ=1 AngleXU=0 Radius=1.55
    g1: LineSegment StartX=1.23043e-11 StartY=2.5 StartZ=0 EndX=-7 EndY=2.5 EndZ=0
    g2: LineSegment StartX=-7 StartY=2.5 StartZ=0 EndX=-7 EndY=-2.5 EndZ=0
    g3: LineSegment StartX=1.23043e-11 StartY=-2.5 StartZ=0 EndX=-7 EndY=-2.5 EndZ=0
    g4: ArcOfCircle CenterX=0 CenterY=0 CenterZ=0 NormalX=0 NormalY=0 NormalZ=1 AngleXU=0 Radius=2.5 StartAngle=4.71239 EndAngle=7.85398
  constraints (14):
    c: Diameter(g0) = 3.1
    c: Horizontal(g1)
    c: Coincident(g2,g1)
    c: Vertical(g2)
    c: Coincident(g3,g2)
    c: Horizontal(g3)
    c: Coincident(g4,g1)
    c: Coincident(g4,g3)
    c: Angle(g4) = 3.14159
    c: Distance(g3,g1) = 5
    c: Vertical(g3,g1)
    c: Coincident(g4,g0)
    c: Coincident(g0,g-1)
    c: Distance(g3) = 7
FEATURE [PartDesign::Pad] Pad
  Direction = (1,1,1)
  Length = 2
  Length2 = 100
  Profile = -> Sketch
  Type = 0
FEATURE [Sketcher::SketchObject] Sketch001
  ExternalGeometry = -> [Pad]
  FullyConstrained = true
  MapMode = 5
  Placement = pos=(0,0,0) rot=(1,0,0;1.5708rad)
  Support = -> [XZ_Plane]
  sketch-geometry (2):
    g0: ArcOfCircle CenterX=-27 CenterY=2.8025e-12 CenterZ=0 NormalX=0 NormalY=0 NormalZ=1 AngleXU=0 Radius=20 StartAngle=-1.33e-14 EndAngle=1.5708
    g1: LineSegment StartX=-27 StartY=20 StartZ=0 EndX=-65 EndY=20 EndZ=0
  constraints (6):
    c: Coincident(g0,g-3)
    c: Horizontal(g1)
    c: DistanceX(g1,g-1) = 65
    c: DistanceY(g-1,g1) = 20
    c: Tangent(g1,g0) = -1.5708
    c: Angle(g0) = 1.5708
FEATURE [Sketcher::SketchObject] Sketch002
  ExternalGeometry = -> [Sketch001]
  FullyConstrained = true
  MapMode = 5
  Support = -> [XY_Plane]
  sketch-geometry (7):
    g0: LineSegment StartX=-8.44338 StartY=-2.5 StartZ=0 EndX=-5.55662 EndY=-2.5 EndZ=0
    g1: LineSegment StartX=-5.55662 StartY=-2.5 StartZ=0 EndX=-4.11325 EndY=-1.24e-14 EndZ=0
    g2: LineSegment StartX=-4.11325 StartY=-1.24e-14 StartZ=0 EndX=-5.55662 EndY=2.5 EndZ=0
    g3: LineSegment StartX=-5.55662 StartY=2.5 StartZ=0 EndX=-8.44338 EndY=2.5 EndZ=0
    g4: LineSegment StartX=-8.44338 StartY=2.5 StartZ=0 EndX=-9.88675 EndY=-1.3e-15 EndZ=0
    g5: LineSegment StartX=-9.88675 StartY=-1.3e-15 StartZ=0 EndX=-8.44338 EndY=-2.5 EndZ=0
    g6: Circle CenterX=-7 CenterY=0 CenterZ=0 NormalX=0 NormalY=0 NormalZ=1 AngleXU=0 Radius=2.88675
  constraints (16):
    c: Coincident(g0,g1)
    c: Coincident(g1,g2)
    c: Coincident(g2,g3)
    c: Coincident(g3,g4)
    c: Coincident(g4,g5)
    c: Coincident(g5,g0)
    c: Equal(g0, g1-g5) x5
    c: PointOnObject(g0,g6)
    c: PointOnObject(g1,g6)
    c: PointOnObject(g2,g6)
    c: PointOnObject(g3,g6)
    c: PointOnObject(g4,g6)
    c: PointOnObject(g5,g6)
    c: Coincident(g6,g-3)
    c: DistanceY(g0,g3) = 5
    c: Horizontal(g0)
FEATURE [PartDesign::AdditivePipe] AdditivePipe
  AuxilleryCurvelinear = true
  AuxillerySpineTangent = false
  BaseFeature = -> Pad
  Binormal = (0,0,0)
  Mode = 0
  Profile = -> Sketch002
  Spine = -> Sketch001
  SpineTangent = false
  Transformation = 0
  Transition = 0
FEATURE [PartDesign::Plane] DatumPlane
  AttachmentOffset = pos=(0,20,0) rot=(0.086994,0.994345,-0.060914;1.92519rad)
  Length = 107.992
  MapMode = 5
  Placement = pos=(-65,2.2e-15,20) rot=(0.974517,0.144186,0.171834;1.77069rad)
  ResizeMode = 0
  Support = -> [AdditivePipe]
  Width = 72.6246
FEATURE [Sketcher::SketchObject] Sketch004
  FullyConstrained = true
  MapMode = 5
  Placement = pos=(-65,7.1e-15,20) rot=(0.974517,0.144186,0.171834;1.77069rad)
  Support = -> [DatumPlane]
  sketch-geometry (4):
    g0: LineSegment StartX=0 StartY=0 StartZ=0 EndX=-2.3 EndY=0 EndZ=0
    g1: LineSegment StartX=-2.3 StartY=0 StartZ=0 EndX=-2 EndY=-9 EndZ=0
    g2: LineSegment StartX=-2 StartY=-9 StartZ=0 EndX=0 EndY=-9 EndZ=0
    g3: LineSegment StartX=0 StartY=-9 StartZ=0 EndX=0 EndY=0 EndZ=0
  constraints (12):
    c: PointOnObject(g0,g-1)
    c: Horizontal(g0)
    c: Coincident(g1,g0)
    c: PointOnObject(g2,g-2)
    c: Vertical(g3)
    c: Distance(g2) = 2
    c: Distance(g0) = 2.3
    c: Coincident(g2,g1)
    c: Coincident(g3,g0)
    c: Coincident(g3,g2)
    c: Distance(g3) = 9
    c: Horizontal(g2)
FEATURE [PartDesign::Revolution] Revolution
  Angle = 360
  Axis = (-1.27e-14,-0.173648,0.984808)
  Base = (-65,3.6e-15,20)
  BaseFeature = -> AdditivePipe
  Profile = -> Sketch004
  ReferenceAxis = -> Sketch004 [V_Axis]
FEATURE [PartDesign::CoordinateSystem] LCS_Hinge
  AttacherType = Attacher::AttachEngine3D
  MapMode = 11
  Placement = pos=(0,0,0) rot=(0,0,1;1.5708rad)
  Support = -> [Revolution]
FEATURE [PartDesign::CoordinateSystem] LCS_Luer
  AttacherType = Attacher::AttachEngine3D
  MapMode = 45
  Placement = pos=(-65,1.56283,11.1367) rot=(1,0,0;0.174533rad)
  Support = -> [Revolution]
FEATURE [PartDesign::Body] Body  label="Arm_tilted_Arena"
  Group = -> [Sketch,Pad,Sketch001,Sketch002,AdditivePipe,DatumPlane,Sketch004,Revolution,LCS_Hinge,LCS_Luer]
  Origin = -> Origin
  Tip = -> Revolution
---- part MicroManipulator_Carriage_Hinge_top.FCStd = doc fcstd_ad225df2d7b6 ----
FCSTD DOCUMENT  (FreeCAD 0.19R24344 (Git))
Label: MicroManipulator_Carriage_Hinge_top
Comment: Carriage for the Z axis (top) with hinges as mount points for an arm. 
License: Creative Commons Attribution-NonCommercial-ShareAlike
LicenseURL: http://creativecommons.org/licenses/by-nc-sa/4.0/
objects: Sketcher::SketchObject×11, PartDesign::Pocket×6, PartDesign::CoordinateSystem×3, PartDesign::Pad×2, PartDesign::Chamfer×1, PartDesign::Body×1, App::Part×1
note: 33 computed .brp shape members not serialized (recipe doc carries the construction recipe); baked Part::Feature solids carry a one-line shape summary decoded from their .brp

FEATURE [Sketcher::SketchObject] Sketch
  FullyConstrained = true
  MapMode = 5
  Placement = pos=(0,0,0) rot=(0.57735,0.57735,0.57735;2.0944rad)
  Support = -> [YZ_Plane]
  sketch-geometry (11):
    g0: LineSegment StartX=-5 StartY=8 StartZ=0 EndX=-5 EndY=10 EndZ=0
    g1: LineSegment StartX=-5 StartY=10 StartZ=0 EndX=5 EndY=10 EndZ=0
    g2: LineSegment StartX=5 StartY=10 StartZ=0 EndX=5 EndY=8 EndZ=0
    g3: LineSegment StartX=5 StartY=3 StartZ=0 EndX=5 EndY=4e-16 EndZ=0
    g4: LineSegment StartX=5 StartY=4e-16 StartZ=0 EndX=2.5 EndY=4e-16 EndZ=0
    g5: LineSegment StartX=-2.5 StartY=-2e-16 StartZ=0 EndX=-5 EndY=-2e-16 EndZ=0
    g6: LineSegment StartX=-5 StartY=-2e-16 StartZ=0 EndX=-5 EndY=3 EndZ=0
    g7: ArcOfCircle CenterX=2e-16 CenterY=-1.44338 CenterZ=0 NormalX=0 NormalY=0 NormalZ=1 AngleXU=0 Radius=2.88675 StartAngle=0.523599 EndAngle=2.61799
    g8: ArcOfCircle CenterX=-6.44338 CenterY=5.5 CenterZ=0 NormalX=0 NormalY=0 NormalZ=1 AngleXU=0 Radius=2.88675 StartAngle=5.23599 EndAngle=7.33038
    g9: ArcOfCircle CenterX=6.44338 CenterY=5.5 CenterZ=0 NormalX=0 NormalY=0 NormalZ=1 AngleXU=0 Radius=2.88675 StartAngle=2.0944 EndAngle=4.18879
    g10: Circle CenterX=0 CenterY=5 CenterZ=0 NormalX=0 NormalY=0 NormalZ=1 AngleXU=0 Radius=1.75
  constraints (34):
    c: Vertical(g0)
    c: Coincident(g1,g0)
    c: Coincident(g2,g1)
    c: Vertical(g2)
    c: Vertical(g3)
    c: Coincident(g4,g3)
    c: Horizontal(g4)
    c: Horizontal(g5)
    c: Coincident(g6,g5)
    c: Vertical(g6)
    c: Coincident(g7,g5)
    c: Coincident(g7,g4)
    c: Coincident(g8,g6)
    c: Coincident(g8,g0)
    c: Coincident(g9,g3)
    c: Coincident(g9,g2)
    c: Vertical(g0,g6)
    c: Vertical(g2,g3)
    c: Angle(g8) = 2.0944
    c: Angle(g9) = 2.0944
    c: Angle(g7) = 2.0944
    c: Distance(g1) = 10
    c: Distance(g5,g4) = 5
    c: Distance(g6,g0) = 5
    c: Distance(g2,g3) = 5
    c: Horizontal(g0,g2)
    c: Symmetric(g1,g0,g-2)
    c: PointOnObject(g3,g-1)
    c: Symmetric(g4,g5,g-2)
    c: Distance(g0,g5) = 10
    c: Distance(g6,g5) = 3
    c: PointOnObject(g10,g-2)
    c: Diameter(g10) = 3.5
    c: DistanceY(g10) = 5
FEATURE [PartDesign::Pad] Pad
  Direction = (1,1,1)
  Length = 21
  Length2 = 100
  Placement = pos=(0,0,0) rot=(0.57735,0.57735,0.57735;2.0944rad)
  Profile = -> Sketch
  Type = 0
FEATURE [Sketcher::SketchObject] Sketch002
  FullyConstrained = true
  MapMode = 5
  Placement = pos=(-3e-15,4e-15,10) rot=(0,0,-1;1.5708rad)
  sketch-geometry (8):
    g0: LineSegment StartX=-2.75 StartY=6.9 StartZ=0 EndX=2.75 EndY=6.9 EndZ=0
    g1: LineSegment StartX=2.75 StartY=6.9 StartZ=0 EndX=2.75 EndY=4.5 EndZ=0
    g2: LineSegment StartX=2.75 StartY=4.5 StartZ=0 EndX=-2.75 EndY=4.5 EndZ=0
    g3: LineSegment StartX=-2.75 StartY=4.5 StartZ=0 EndX=-2.75 EndY=6.9 EndZ=0
    g4: LineSegment StartX=-2.75 StartY=19.4 StartZ=0 EndX=2.75 EndY=19.4 EndZ=0
    g5: LineSegment StartX=2.75 StartY=19.4 StartZ=0 EndX=2.75 EndY=17 EndZ=0
    g6: LineSegment StartX=2.75 StartY=17 StartZ=0 EndX=-2.75 EndY=17 EndZ=0
    g7: LineSegment StartX=-2.75 StartY=17 StartZ=0 EndX=-2.75 EndY=19.4 EndZ=0
  constraints (22):
    c: Coincident(g0,g1)
    c: Coincident(g1,g2)
    c: Coincident(g2,g3)
    c: Coincident(g3,g0)
    c: Horizontal(g2)
    c: Vertical(g1)
    c: Vertical(g3)
    c: Distance(g3) = 2.4
    c: Distance(g0) = 5.5
    c: Symmetric(g0,g0,g-2)
    c: DistanceY(g-1,g1) = 4.5
    c: Coincident(g4,g5)
    c: Coincident(g5,g6)
    c: Coincident(g6,g7)
    c: Coincident(g7,g4)
    c: Horizontal(g6)
    c: Vertical(g5)
    c: Vertical(g7)
    c: Distance(g7) = 2.4
    c: Distance(g4) = 5.5
    c: Symmetric(g4,g4,g-2)
    c: DistanceY(g-1,g5) = 17
FEATURE [PartDesign::Pocket] Pocket
  BaseFeature = -> Pad
  Length = 8
  Length2 = 100
  Placement = pos=(0,0,0) rot=(0.57735,0.57735,0.57735;2.0944rad)
  Profile = -> Sketch002
  Type = 0
FEATURE [Sketcher::SketchObject] Sketch003
  FullyConstrained = true
  MapMode = 5
  Placement = pos=(0,0,0) rot=(0.57735,0.57735,-0.57735;4.18879rad)
  Support = -> [Pocket]
  sketch-geometry (1):
    g0: Circle CenterX=0 CenterY=-5 CenterZ=0 NormalX=0 NormalY=0 NormalZ=1 AngleXU=0 Radius=3.1
  constraints (3):
    c: PointOnObject(g0,g-2)
    c: Diameter(g0) = 6.2
    c: DistanceY(g0,g-1) = 5
FEATURE [PartDesign::Pocket] Pocket001
  BaseFeature = -> Pocket
  Length = 3
  Length2 = 100
  Placement = pos=(0,0,0) rot=(0.57735,0.57735,0.57735;2.0944rad)
  Profile = -> Sketch003
  Type = 0
FEATURE [PartDesign::CoordinateSystem] LCS_0
  AttacherType = Attacher::AttachEngine3D
  MapMode = 2
  Support = -> [X_Axis001]
FEATURE [Sketcher::SketchObject] Sketch004
  FullyConstrained = true
  MapMode = 5
  Placement = pos=(21,-4.6e-15,4.6e-15) rot=(0.57735,0.57735,0.57735;2.0944rad)
  Support = -> [Pocket001]
FEATURE [Sketcher::SketchObject] Sketch005
  FullyConstrained = true
  MapMode = 5
  Placement = pos=(21,-4.6e-15,4.6e-15) rot=(0.57735,0.57735,0.57735;2.0944rad)
  Support = -> [Pocket001]
FEATURE [Sketcher::SketchObject] Sketch006
  FullyConstrained = true
  MapMode = 5
  Placement = pos=(0,0,0) rot=(0.57735,0.57735,-0.57735;4.18879rad)
  Support = -> [Pocket001]
FEATURE [Sketcher::SketchObject] Sketch007
  FullyConstrained = true
  MapMode = 5
  Placement = pos=(0,0,0) rot=(0.57735,0.57735,-0.57735;4.18879rad)
  Support = -> [Pocket001]
  sketch-geometry (16):
    g0: LineSegment StartX=-4.25 StartY=-0.75 StartZ=0 EndX=-2.75 EndY=-0.75 EndZ=0
    g1: LineSegment StartX=-2.75 StartY=-0.75 StartZ=0 EndX=-2.75 EndY=-2.75 EndZ=0
    g2: LineSegment StartX=-2.75 StartY=-2.75 StartZ=0 EndX=-4.25 EndY=-2.75 EndZ=0
    g3: LineSegment StartX=-4.25 StartY=-2.75 StartZ=0 EndX=-4.25 EndY=-0.75 EndZ=0
    g4: LineSegment StartX=2.75 StartY=-0.75 StartZ=0 EndX=4.25 EndY=-0.75 EndZ=0
    g5: LineSegment StartX=4.25 StartY=-0.75 StartZ=0 EndX=4.25 EndY=-2.75 EndZ=0
    g6: LineSegment StartX=4.25 StartY=-2.75 StartZ=0 EndX=2.75 EndY=-2.75 EndZ=0
    g7: LineSegment StartX=2.75 StartY=-2.75 StartZ=0 EndX=2.75 EndY=-0.75 EndZ=0
    g8: LineSegment StartX=-4 StartY=-8 StartZ=0 EndX=-1.5 EndY=-8 EndZ=0
    g9: LineSegment StartX=-1.5 StartY=-8 StartZ=0 EndX=-1.5 EndY=-9.5 EndZ=0
    g10: LineSegment StartX=-1.5 StartY=-9.5 StartZ=0 EndX=-4 EndY=-9.5 EndZ=0
    g11: LineSegment StartX=-4 StartY=-9.5 StartZ=0 EndX=-4 EndY=-8 EndZ=0
    g12: LineSegment StartX=1.5 StartY=-8 StartZ=0 EndX=4 EndY=-8 EndZ=0
    g13: LineSegment StartX=4 StartY=-8 StartZ=0 EndX=4 EndY=-9.5 EndZ=0
    g14: LineSegment StartX=4 StartY=-9.5 StartZ=0 EndX=1.5 EndY=-9.5 EndZ=0
    g15: LineSegment StartX=1.5 StartY=-9.5 StartZ=0 EndX=1.5 EndY=-8 EndZ=0
  constraints (48):
    c: Coincident(g0,g1)
    c: Coincident(g1,g2)
    c: Coincident(g2,g3)
    c: Coincident(g3,g0)
    c: Horizontal(g0)
    c: Horizontal(g2)
    c: Vertical(g1)
    c: Vertical(g3)
    c: Distance(g0) = 1.5
    c: Distance(g3) = 2
    c: DistanceY(g0,g-1) = 0.75
    c: DistanceX(g0,g-1) = 2.75
    c: Coincident(g4,g5)
    c: Coincident(g5,g6)
    c: Coincident(g6,g7)
    c: Coincident(g7,g4)
    c: Horizontal(g4)
    c: Horizontal(g6)
    c: Vertical(g5)
    c: Vertical(g7)
    c: Distance(g4) = 1.5
    c: Distance(g7) = 2
    c: DistanceY(g4,g-1) = 0.75
    c: DistanceX(g-1,g4) = 2.75
    c: Coincident(g8,g9)
    c: Coincident(g9,g10)
    c: Coincident(g10,g11)
    c: Coincident(g11,g8)
    c: Horizontal(g8)
    c: Horizontal(g10)
    c: Vertical(g9)
    c: Vertical(g11)
    c: Coincident(g12,g13)
    c: Coincident(g13,g14)
    c: Coincident(g14,g15)
    c: Coincident(g15,g12)
    c: Horizontal(g12)
    c: Horizontal(g14)
    c: Vertical(g13)
    c: Vertical(g15)
    c: Distance(g10) = 2.5
    c: Distance(g14) = 2.5
    c: Distance(g9) = 1.5
    c: Distance(g15) = 1.5
    c: DistanceX(g8,g-1) = 1.5
    c: DistanceX(g-1,g12) = 1.5
    c: Horizontal(g12,g8)
    c: DistanceY(g8,g-1) = 8
FEATURE [PartDesign::Pocket] Pocket002
  BaseFeature = -> Pocket001
  Length = 5
  Length2 = 100
  Placement = pos=(0,0,0) rot=(0.57735,0.57735,0.57735;2.0944rad)
  Profile = -> Sketch007
  Type = 1
FEATURE [Sketcher::SketchObject] Sketch008
  ExternalGeometry = -> [Pocket002]
  FullyConstrained = true
  MapMode = 5
  Placement = pos=(-2.8e-15,4.4e-15,10) rot=(0,0,-1;1.5708rad)
  Support = -> [Pocket002]
  sketch-geometry (4):
    g0: LineSegment StartX=-5 StartY=16 StartZ=0 EndX=5 EndY=16 EndZ=0
    g1: LineSegment StartX=5 StartY=16 StartZ=0 EndX=5 EndY=8 EndZ=0
    g2: LineSegment StartX=5 StartY=8 StartZ=0 EndX=-5 EndY=8 EndZ=0
    g3: LineSegment StartX=-5 StartY=8 StartZ=0 EndX=-5 EndY=16 EndZ=0
  constraints (12):
    c: Coincident(g0,g1)
    c: Coincident(g1,g2)
    c: Coincident(g2,g3)
    c: Coincident(g3,g0)
    c: Horizontal(g0)
    c: Horizontal(g2)
    c: Vertical(g1)
    c: Vertical(g3)
    c: PointOnObject(g0,g-3)
    c: PointOnObject(g0,g-4)
    c: DistanceY(g0,g-4) = 5
    c: DistanceY(g-4,g1) = 8
FEATURE [PartDesign::Pad] Pad001
  BaseFeature = -> Pocket002
  Direction = (1,1,1)
  Length = 10
  Length2 = 100
  Placement = pos=(0,0,0) rot=(0.57735,0.57735,0.57735;2.0944rad)
  Profile = -> Sketch008
  Type = 0
FEATURE [PartDesign::Chamfer] Chamfer
  Angle = 45
  Base = -> Pad001 [Edge19,Edge112]
  BaseFeature = -> Pad001
  ChamferType = 0
  FlipDirection = false
  Placement = pos=(0,0,0) rot=(0.57735,0.57735,0.57735;2.0944rad)
  Size = 4
  Size2 = 1
  SupportTransform = false
FEATURE [Sketcher::SketchObject] Sketch009
  ExternalGeometry = -> [Chamfer]
  FullyConstrained = true
  MapMode = 5
  Placement = pos=(8,9e-16,2.2e-15) rot=(0.57735,0.57735,-0.57735;4.18879rad)
  Support = -> [Chamfer]
  sketch-geometry (1):
    g0: Circle CenterX=0 CenterY=-17 CenterZ=0 NormalX=0 NormalY=0 NormalZ=1 AngleXU=0 Radius=1.55
  constraints (3):
    c: PointOnObject(g0,g-2)
    c: Diameter(g0) = 3.1
    c: DistanceY(g-3,g0) = 3
FEATURE [PartDesign::Pocket] Pocket003
  BaseFeature = -> Chamfer
  Length = 5
  Length2 = 100
  Placement = pos=(0,0,0) rot=(0.57735,0.57735,0.57735;2.0944rad)
  Profile = -> Sketch009
  Type = 1
FEATURE [Sketcher::SketchObject] Sketch010
  ExternalGeometry = -> [Pocket003]
  FullyConstrained = true
  MapMode = 5
  Placement = pos=(16,1.8e-15,4.5e-15) rot=(0.57735,0.57735,0.57735;2.0944rad)
  Support = -> [Pocket003]
  sketch-geometry (7):
    g0: LineSegment StartX=3.17543 StartY=17 StartZ=0 EndX=1.58771 EndY=19.75 EndZ=0
    g1: LineSegment StartX=1.58771 StartY=19.75 StartZ=0 EndX=-1.58771 EndY=19.75 EndZ=0
    g2: LineSegment StartX=-1.58771 StartY=19.75 StartZ=0 EndX=-3.17543 EndY=17 EndZ=0
    g3: LineSegment StartX=-3.17543 StartY=17 StartZ=0 EndX=-1.58771 EndY=14.25 EndZ=0
    g4: LineSegment StartX=-1.58771 StartY=14.25 StartZ=0 EndX=1.58771 EndY=14.25 EndZ=0
    g5: LineSegment StartX=1.58771 StartY=14.25 StartZ=0 EndX=3.17543 EndY=17 EndZ=0
    g6: Circle CenterX=6.7e-15 CenterY=17 CenterZ=0 NormalX=0 NormalY=0 NormalZ=1 AngleXU=0 Radius=3.17543
  constraints (16):
    c: Coincident(g0,g1)
    c: Coincident(g1,g2)
    c: Coincident(g2,g3)
    c: Coincident(g3,g4)
    c: Coincident(g4,g5)
    c: Coincident(g5,g0)
    c: Equal(g0, g1-g5) x5
    c: PointOnObject(g0,g6)
    c: PointOnObject(g1,g6)
    c: PointOnObject(g2,g6)
    c: PointOnObject(g3,g6)
    c: PointOnObject(g4,g6)
    c: PointOnObject(g5,g6)
    c: Coincident(g6,g-3)
    c: Distance(g1,g0) = 5.5
    c: Horizontal(g1)
FEATURE [PartDesign::Pocket] Pocket004
  BaseFeature = -> Pocket003
  Length = 1
  Length2 = 100
  Placement = pos=(0,0,0) rot=(0.57735,0.57735,0.57735;2.0944rad)
  Profile = -> Sketch010
  Type = 0
FEATURE [Sketcher::SketchObject] Sketch011
  ExternalGeometry = -> [Pocket004]
  FullyConstrained = true
  MapMode = 5
  Placement = pos=(-6.6e-15,8.8e-15,20) rot=(0,0,-1;1.5708rad)
  Support = -> [Pocket004]
  sketch-geometry (4):
    g0: LineSegment StartX=-5 StartY=12.5 StartZ=0 EndX=5 EndY=12.5 EndZ=0
    g1: LineSegment StartX=5 StartY=12.5 StartZ=0 EndX=5 EndY=10.5 EndZ=0
    g2: LineSegment StartX=5 StartY=10.5 StartZ=0 EndX=-5 EndY=10.5 EndZ=0
    g3: LineSegment StartX=-5 StartY=10.5 StartZ=0 EndX=-5 EndY=12.5 EndZ=0
  constraints (12):
    c: Coincident(g0,g1)
    c: Coincident(g1,g2)
    c: Coincident(g2,g3)
    c: Coincident(g3,g0)
    c: Horizontal(g0)
    c: Horizontal(g2)
    c: Vertical(g1)
    c: Vertical(g3)
    c: PointOnObject(g0,g-5)
    c: PointOnObject(g1,g-4)
    c: DistanceY(g-3,g1) = 2.5
    c: Distance(g1) = 2
FEATURE [PartDesign::Pocket] Pocket005
  BaseFeature = -> Pocket004
  Length = 7
  Length2 = 100
  Placement = pos=(0,0,0) rot=(0.57735,0.57735,0.57735;2.0944rad)
  Profile = -> Sketch011
  Type = 0
FEATURE [PartDesign::Body] Body
  Group = -> [Sketch,Pad,Sketch002,Pocket,Sketch003,Pocket001,Sketch004,Sketch005,Sketch006,Sketch007,Pocket002,Sketch008,Pad001,Chamfer,Sketch009,Pocket003,Sketch010,Pocket004,Sketch011,Pocket005]
  Origin = -> Origin
  Tip = -> Pocket005
FEATURE [PartDesign::CoordinateSystem] Screw_LCS
  AttacherType = Attacher::AttachEngine3D
  MapMode = 45
  Placement = pos=(-2e-15,1.47e-14,5) rot=(0.57735,0.57735,0.57735;2.0944rad)
  Support = -> [Pocket005]
FEATURE [PartDesign::CoordinateSystem] ArmMount_LCS
  AttacherType = Attacher::AttachEngine3D
  AttachmentOffset = pos=(0,0,0) rot=(0,1,0;3.14159rad)
  MapMode = 45
  Placement = pos=(12.5,1.35e-14,17) rot=(-0.57735,0.57735,0.57735;4.18879rad)
  Support = -> [Pocket005]
FEATURE [App::Part] Slider  label="Carriage_top"
  Group = -> [LCS_0,Body,Screw_LCS,ArmMount_LCS]
  Origin = -> Origin001
---- part MicroManipulator_Carriage_bottom-center.FCStd = doc fcstd_f369934bd94b ----
FCSTD DOCUMENT  (FreeCAD 0.19R24344 (Git))
Label: MicroManipulator_Carriage_bottom-center
Comment: This is the carriage for X and Y axis of the MicroManipulator. This is derived from the Carriage (combination of 2).
License: Creative Commons Attribution-NonCommercial-ShareAlike
LicenseURL: http://creativecommons.org/licenses/by-nc-sa/4.0/
objects: Sketcher::SketchObject×14, PartDesign::Pocket×6, PartDesign::CoordinateSystem×3, PartDesign::Pad×2, PartDesign::Body×2, Part::MultiFuse×1, App::Part×1
note: 36 computed .brp shape members not serialized (recipe doc carries the construction recipe); baked Part::Feature solids carry a one-line shape summary decoded from their .brp

FEATURE [Sketcher::SketchObject] Sketch
  FullyConstrained = true
  MapMode = 5
  Placement = pos=(0,0,0) rot=(0.57735,0.57735,0.57735;2.0944rad)
  Support = -> [YZ_Plane001]
  sketch-geometry (11):
    g0: LineSegment StartX=-5 StartY=8 StartZ=0 EndX=-5 EndY=10 EndZ=0
    g1: LineSegment StartX=-5 StartY=10 StartZ=0 EndX=5 EndY=10 EndZ=0
    g2: LineSegment StartX=5 StartY=10 StartZ=0 EndX=5 EndY=8 EndZ=0
    g3: LineSegment StartX=5 StartY=3 StartZ=0 EndX=5 EndY=4e-16 EndZ=0
    g4: LineSegment StartX=5 StartY=4e-16 StartZ=0 EndX=2.5 EndY=4e-16 EndZ=0
    g5: LineSegment StartX=-2.5 StartY=-2e-16 StartZ=0 EndX=-5 EndY=-2e-16 EndZ=0
    g6: LineSegment StartX=-5 StartY=-2e-16 StartZ=0 EndX=-5 EndY=3 EndZ=0
    g7: ArcOfCircle CenterX=2e-16 CenterY=-1.44338 CenterZ=0 NormalX=0 NormalY=0 NormalZ=1 AngleXU=0 Radius=2.88675 StartAngle=0.523599 EndAngle=2.61799
    g8: ArcOfCircle CenterX=-6.44338 CenterY=5.5 CenterZ=0 NormalX=0 NormalY=0 NormalZ=1 AngleXU=0 Radius=2.88675 StartAngle=5.23599 EndAngle=7.33038
    g9: ArcOfCircle CenterX=6.44338 CenterY=5.5 CenterZ=0 NormalX=0 NormalY=0 NormalZ=1 AngleXU=0 Radius=2.88675 StartAngle=2.0944 EndAngle=4.18879
    g10: Circle CenterX=0 CenterY=5 CenterZ=0 NormalX=0 NormalY=0 NormalZ=1 AngleXU=0 Radius=1.75
  constraints (34):
    c: Vertical(g0)
    c: Coincident(g1,g0)
    c: Coincident(g2,g1)
    c: Vertical(g2)
    c: Vertical(g3)
    c: Coincident(g4,g3)
    c: Horizontal(g4)
    c: Horizontal(g5)
    c: Coincident(g6,g5)
    c: Vertical(g6)
    c: Coincident(g7,g5)
    c: Coincident(g7,g4)
    c: Coincident(g8,g6)
    c: Coincident(g8,g0)
    c: Coincident(g9,g3)
    c: Coincident(g9,g2)
    c: Vertical(g0,g6)
    c: Vertical(g2,g3)
    c: Angle(g8) = 2.0944
    c: Angle(g9) = 2.0944
    c: Angle(g7) = 2.0944
    c: Distance(g1) = 10
    c: Distance(g5,g4) = 5
    c: Distance(g6,g0) = 5
    c: Distance(g2,g3) = 5
    c: Horizontal(g0,g2)
    c: Symmetric(g1,g0,g-2)
    c: PointOnObject(g3,g-1)
    c: Symmetric(g4,g5,g-2)
    c: Distance(g0,g5) = 10
    c: Distance(g6,g5) = 3
    c: PointOnObject(g10,g-2)
    c: Diameter(g10) = 3.5
    c: DistanceY(g10) = 5
FEATURE [PartDesign::Pad] Pad
  Direction = (1,1,1)
  Length = 21
  Length2 = 100
  Placement = pos=(0,0,0) rot=(0.57735,0.57735,0.57735;2.0944rad)
  Profile = -> Sketch
  Type = 0
FEATURE [Sketcher::SketchObject] Sketch002
  FullyConstrained = true
  MapMode = 5
  Placement = pos=(-3e-15,4e-15,10) rot=(0,0,-1;1.5708rad)
  sketch-geometry (8):
    g0: LineSegment StartX=-2.75 StartY=6.9 StartZ=0 EndX=2.75 EndY=6.9 EndZ=0
    g1: LineSegment StartX=2.75 StartY=6.9 StartZ=0 EndX=2.75 EndY=4.5 EndZ=0
    g2: LineSegment StartX=2.75 StartY=4.5 StartZ=0 EndX=-2.75 EndY=4.5 EndZ=0
    g3: LineSegment StartX=-2.75 StartY=4.5 StartZ=0 EndX=-2.75 EndY=6.9 EndZ=0
    g4: LineSegment StartX=-2.75 StartY=19.4 StartZ=0 EndX=2.75 EndY=19.4 EndZ=0
    g5: LineSegment StartX=2.75 StartY=19.4 StartZ=0 EndX=2.75 EndY=17 EndZ=0
    g6: LineSegment StartX=2.75 StartY=17 StartZ=0 EndX=-2.75 EndY=17 EndZ=0
    g7: LineSegment StartX=-2.75 StartY=17 StartZ=0 EndX=-2.75 EndY=19.4 EndZ=0
  constraints (22):
    c: Coincident(g0,g1)
    c: Coincident(g1,g2)
    c: Coincident(g2,g3)
    c: Coincident(g3,g0)
    c: Horizontal(g2)
    c: Vertical(g1)
    c: Vertical(g3)
    c: Distance(g3) = 2.4
    c: Distance(g0) = 5.5
    c: Symmetric(g0,g0,g-2)
    c: DistanceY(g-1,g1) = 4.5
    c: Coincident(g4,g5)
    c: Coincident(g5,g6)
    c: Coincident(g6,g7)
    c: Coincident(g7,g4)
    c: Horizontal(g6)
    c: Vertical(g5)
    c: Vertical(g7)
    c: Distance(g7) = 2.4
    c: Distance(g4) = 5.5
    c: Symmetric(g4,g4,g-2)
    c: DistanceY(g-1,g5) = 17
FEATURE [PartDesign::Pocket] Pocket
  BaseFeature = -> Pad
  Length = 8
  Length2 = 100
  Placement = pos=(0,0,0) rot=(0.57735,0.57735,0.57735;2.0944rad)
  Profile = -> Sketch002
  Type = 0
FEATURE [Sketcher::SketchObject] Sketch003
  FullyConstrained = true
  MapMode = 5
  Placement = pos=(0,0,0) rot=(0.57735,0.57735,-0.57735;4.18879rad)
  Support = -> [Pocket]
  sketch-geometry (1):
    g0: Circle CenterX=0 CenterY=-5 CenterZ=0 NormalX=0 NormalY=0 NormalZ=1 AngleXU=0 Radius=3.1
  constraints (3):
    c: PointOnObject(g0,g-2)
    c: Diameter(g0) = 6.2
    c: DistanceY(g0,g-1) = 5
FEATURE [PartDesign::Pocket] Pocket001
  BaseFeature = -> Pocket
  Length = 3
  Length2 = 100
  Placement = pos=(0,0,0) rot=(0.57735,0.57735,0.57735;2.0944rad)
  Profile = -> Sketch003
  Type = 0
FEATURE [Sketcher::SketchObject] Sketch004
  FullyConstrained = true
  MapMode = 5
  Placement = pos=(21,-4.6e-15,4.6e-15) rot=(0.57735,0.57735,0.57735;2.0944rad)
  Support = -> [Pocket001]
FEATURE [Sketcher::SketchObject] Sketch005
  FullyConstrained = true
  MapMode = 5
  Placement = pos=(21,-4.6e-15,4.6e-15) rot=(0.57735,0.57735,0.57735;2.0944rad)
  Support = -> [Pocket001]
FEATURE [Sketcher::SketchObject] Sketch006
  FullyConstrained = true
  MapMode = 5
  Placement = pos=(0,0,0) rot=(0.57735,0.57735,-0.57735;4.18879rad)
  Support = -> [Pocket001]
FEATURE [Sketcher::SketchObject] Sketch007
  FullyConstrained = true
  MapMode = 5
  Placement = pos=(0,0,0) rot=(0.57735,0.57735,-0.57735;4.18879rad)
  Support = -> [Pocket001]
  sketch-geometry (16):
    g0: LineSegment StartX=-4.25 StartY=-0.75 StartZ=0 EndX=-2.75 EndY=-0.75 EndZ=0
    g1: LineSegment StartX=-2.75 StartY=-0.75 StartZ=0 EndX=-2.75 EndY=-2.75 EndZ=0
    g2: LineSegment StartX=-2.75 StartY=-2.75 StartZ=0 EndX=-4.25 EndY=-2.75 EndZ=0
    g3: LineSegment StartX=-4.25 StartY=-2.75 StartZ=0 EndX=-4.25 EndY=-0.75 EndZ=0
    g4: LineSegment StartX=2.75 StartY=-0.75 StartZ=0 EndX=4.25 EndY=-0.75 EndZ=0
    g5: LineSegment StartX=4.25 StartY=-0.75 StartZ=0 EndX=4.25 EndY=-2.75 EndZ=0
    g6: LineSegment StartX=4.25 StartY=-2.75 StartZ=0 EndX=2.75 EndY=-2.75 EndZ=0
    g7: LineSegment StartX=2.75 StartY=-2.75 StartZ=0 EndX=2.75 EndY=-0.75 EndZ=0
    g8: LineSegment StartX=-4 StartY=-8 StartZ=0 EndX=-1.5 EndY=-8 EndZ=0
    g9: LineSegment StartX=-1.5 StartY=-8 StartZ=0 EndX=-1.5 EndY=-9.5 EndZ=0
    g10: LineSegment StartX=-1.5 StartY=-9.5 StartZ=0 EndX=-4 EndY=-9.5 EndZ=0
    g11: LineSegment StartX=-4 StartY=-9.5 StartZ=0 EndX=-4 EndY=-8 EndZ=0
    g12: LineSegment StartX=1.5 StartY=-8 StartZ=0 EndX=4 EndY=-8 EndZ=0
    g13: LineSegment StartX=4 StartY=-8 StartZ=0 EndX=4 EndY=-9.5 EndZ=0
    g14: LineSegment StartX=4 StartY=-9.5 StartZ=0 EndX=1.5 EndY=-9.5 EndZ=0
    g15: LineSegment StartX=1.5 StartY=-9.5 StartZ=0 EndX=1.5 EndY=-8 EndZ=0
  constraints (48):
    c: Coincident(g0,g1)
    c: Coincident(g1,g2)
    c: Coincident(g2,g3)
    c: Coincident(g3,g0)
    c: Horizontal(g0)
    c: Horizontal(g2)
    c: Vertical(g1)
    c: Vertical(g3)
    c: Distance(g0) = 1.5
    c: Distance(g3) = 2
    c: DistanceY(g0,g-1) = 0.75
    c: DistanceX(g0,g-1) = 2.75
    c: Coincident(g4,g5)
    c: Coincident(g5,g6)
    c: Coincident(g6,g7)
    c: Coincident(g7,g4)
    c: Horizontal(g4)
    c: Horizontal(g6)
    c: Vertical(g5)
    c: Vertical(g7)
    c: Distance(g4) = 1.5
    c: Distance(g7) = 2
    c: DistanceY(g4,g-1) = 0.75
    c: DistanceX(g-1,g4) = 2.75
    c: Coincident(g8,g9)
    c: Coincident(g9,g10)
    c: Coincident(g10,g11)
    c: Coincident(g11,g8)
    c: Horizontal(g8)
    c: Horizontal(g10)
    c: Vertical(g9)
    c: Vertical(g11)
    c: Coincident(g12,g13)
    c: Coincident(g13,g14)
    c: Coincident(g14,g15)
    c: Coincident(g15,g12)
    c: Horizontal(g12)
    c: Horizontal(g14)
    c: Vertical(g13)
    c: Vertical(g15)
    c: Distance(g10) = 2.5
    c: Distance(g14) = 2.5
    c: Distance(g9) = 1.5
    c: Distance(g15) = 1.5
    c: DistanceX(g8,g-1) = 1.5
    c: DistanceX(g-1,g12) = 1.5
    c: Horizontal(g12,g8)
    c: DistanceY(g8,g-1) = 8
FEATURE [PartDesign::Pocket] Pocket002
  BaseFeature = -> Pocket001
  Length = 5
  Length2 = 100
  Placement = pos=(0,0,0) rot=(0.57735,0.57735,0.57735;2.0944rad)
  Profile = -> Sketch007
  Type = 1
FEATURE [PartDesign::Body] Body001
  Group = -> [Sketch,Pad,Sketch002,Pocket,Sketch003,Pocket001,Sketch004,Sketch005,Sketch006,Sketch007,Pocket002]
  Origin = -> Origin001
  Tip = -> Pocket002
FEATURE [Sketcher::SketchObject] Sketch008
  FullyConstrained = true
  MapMode = 5
  Placement = pos=(0,0,0) rot=(0.57735,0.57735,0.57735;2.0944rad)
  Support = -> [YZ_Plane002]
  sketch-geometry (11):
    g0: LineSegment StartX=-5 StartY=8 StartZ=0 EndX=-5 EndY=10 EndZ=0
    g1: LineSegment StartX=-5 StartY=10 StartZ=0 EndX=5 EndY=10 EndZ=0
    g2: LineSegment StartX=5 StartY=10 StartZ=0 EndX=5 EndY=8 EndZ=0
    g3: LineSegment StartX=5 StartY=3 StartZ=0 EndX=5 EndY=4e-16 EndZ=0
    g4: LineSegment StartX=5 StartY=4e-16 StartZ=0 EndX=2.5 EndY=4e-16 EndZ=0
    g5: LineSegment StartX=-2.5 StartY=-2e-16 StartZ=0 EndX=-5 EndY=-2e-16 EndZ=0
    g6: LineSegment StartX=-5 StartY=-2e-16 StartZ=0 EndX=-5 EndY=3 EndZ=0
    g7: ArcOfCircle CenterX=2e-16 CenterY=-1.44338 CenterZ=0 NormalX=0 NormalY=0 NormalZ=1 AngleXU=0 Radius=2.88675 StartAngle=0.523599 EndAngle=2.61799
    g8: ArcOfCircle CenterX=-6.44338 CenterY=5.5 CenterZ=0 NormalX=0 NormalY=0 NormalZ=1 AngleXU=0 Radius=2.88675 StartAngle=5.23599 EndAngle=7.33038
    g9: ArcOfCircle CenterX=6.44338 CenterY=5.5 CenterZ=0 NormalX=0 NormalY=0 NormalZ=1 AngleXU=0 Radius=2.88675 StartAngle=2.0944 EndAngle=4.18879
    g10: Circle CenterX=0 CenterY=5 CenterZ=0 NormalX=0 NormalY=0 NormalZ=1 AngleXU=0 Radius=1.75
  constraints (34):
    c: Vertical(g0)
    c: Coincident(g1,g0)
    c: Coincident(g2,g1)
    c: Vertical(g2)
    c: Vertical(g3)
    c: Coincident(g4,g3)
    c: Horizontal(g4)
    c: Horizontal(g5)
    c: Coincident(g6,g5)
    c: Vertical(g6)
    c: Coincident(g7,g5)
    c: Coincident(g7,g4)
    c: Coincident(g8,g6)
    c: Coincident(g8,g0)
    c: Coincident(g9,g3)
    c: Coincident(g9,g2)
    c: Vertical(g0,g6)
    c: Vertical(g2,g3)
    c: Angle(g8) = 2.0944
    c: Angle(g9) = 2.0944
    c: Angle(g7) = 2.0944
    c: Distance(g1) = 10
    c: Distance(g5,g4) = 5
    c: Distance(g6,g0) = 5
    c: Distance(g2,g3) = 5
    c: Horizontal(g0,g2)
    c: Symmetric(g1,g0,g-2)
    c: PointOnObject(g3,g-1)
    c: Symmetric(g4,g5,g-2)
    c: Distance(g0,g5) = 10
    c: Distance(g6,g5) = 3
    c: PointOnObject(g10,g-2)
    c: Diameter(g10) = 3.5
    c: DistanceY(g10) = 5
FEATURE [PartDesign::Pad] Pad001
  Direction = (1,1,1)
  Length = 21
  Length2 = 100
  Placement = pos=(0,0,0) rot=(0.57735,0.57735,0.57735;2.0944rad)
  Profile = -> Sketch008
  Type = 0
FEATURE [Sketcher::SketchObject] Sketch009
  FullyConstrained = true
  MapMode = 5
  Placement = pos=(-3e-15,4e-15,10) rot=(0,0,-1;1.5708rad)
  sketch-geometry (8):
    g0: LineSegment StartX=-2.75 StartY=6.9 StartZ=0 EndX=2.75 EndY=6.9 EndZ=0
    g1: LineSegment StartX=2.75 StartY=6.9 StartZ=0 EndX=2.75 EndY=4.5 EndZ=0
    g2: LineSegment StartX=2.75 StartY=4.5 StartZ=0 EndX=-2.75 EndY=4.5 EndZ=0
    g3: LineSegment StartX=-2.75 StartY=4.5 StartZ=0 EndX=-2.75 EndY=6.9 EndZ=0
    g4: LineSegment StartX=-2.75 StartY=19.4 StartZ=0 EndX=2.75 EndY=19.4 EndZ=0
    g5: LineSegment StartX=2.75 StartY=19.4 StartZ=0 EndX=2.75 EndY=17 EndZ=0
    g6: LineSegment StartX=2.75 StartY=17 StartZ=0 EndX=-2.75 EndY=17 EndZ=0
    g7: LineSegment StartX=-2.75 StartY=17 StartZ=0 EndX=-2.75 EndY=19.4 EndZ=0
  constraints (22):
    c: Coincident(g0,g1)
    c: Coincident(g1,g2)
    c: Coincident(g2,g3)
    c: Coincident(g3,g0)
    c: Horizontal(g2)
    c: Vertical(g1)
    c: Vertical(g3)
    c: Distance(g3) = 2.4
    c: Distance(g0) = 5.5
    c: Symmetric(g0,g0,g-2)
    c: DistanceY(g-1,g1) = 4.5
    c: Coincident(g4,g5)
    c: Coincident(g5,g6)
    c: Coincident(g6,g7)
    c: Coincident(g7,g4)
    c: Horizontal(g6)
    c: Vertical(g5)
    c: Vertical(g7)
    c: Distance(g7) = 2.4
    c: Distance(g4) = 5.5
    c: Symmetric(g4,g4,g-2)
    c: DistanceY(g-1,g5) = 17
FEATURE [PartDesign::Pocket] Pocket003
  BaseFeature = -> Pad001
  Length = 8
  Length2 = 100
  Placement = pos=(0,0,0) rot=(0.57735,0.57735,0.57735;2.0944rad)
  Profile = -> Sketch009
  Type = 0
FEATURE [Sketcher::SketchObject] Sketch010
  FullyConstrained = true
  MapMode = 5
  Placement = pos=(0,0,0) rot=(0.57735,0.57735,-0.57735;4.18879rad)
  Support = -> [Pocket003]
  sketch-geometry (1):
    g0: Circle CenterX=0 CenterY=-5 CenterZ=0 NormalX=0 NormalY=0 NormalZ=1 AngleXU=0 Radius=3.1
  constraints (3):
    c: PointOnObject(g0,g-2)
    c: Diameter(g0) = 6.2
    c: DistanceY(g0,g-1) = 5
FEATURE [PartDesign::Pocket] Pocket004
  BaseFeature = -> Pocket003
  Length = 3
  Length2 = 100
  Placement = pos=(0,0,0) rot=(0.57735,0.57735,0.57735;2.0944rad)
  Profile = -> Sketch010
  Type = 0
FEATURE [Sketcher::SketchObject] Sketch011
  FullyConstrained = true
  MapMode = 5
  Placement = pos=(21,-4.6e-15,4.6e-15) rot=(0.57735,0.57735,0.57735;2.0944rad)
  Support = -> [Pocket004]
FEATURE [Sketcher::SketchObject] Sketch012
  FullyConstrained = true
  MapMode = 5
  Placement = pos=(21,-4.6e-15,4.6e-15) rot=(0.57735,0.57735,0.57735;2.0944rad)
  Support = -> [Pocket004]
FEATURE [Sketcher::SketchObject] Sketch013
  FullyConstrained = true
  MapMode = 5
  Placement = pos=(0,0,0) rot=(0.57735,0.57735,-0.57735;4.18879rad)
  Support = -> [Pocket004]
FEATURE [Sketcher::SketchObject] Sketch014
  FullyConstrained = true
  MapMode = 5
  Placement = pos=(0,0,0) rot=(0.57735,0.57735,-0.57735;4.18879rad)
  Support = -> [Pocket004]
  sketch-geometry (16):
    g0: LineSegment StartX=-4.25 StartY=-0.75 StartZ=0 EndX=-2.75 EndY=-0.75 EndZ=0
    g1: LineSegment StartX=-2.75 StartY=-0.75 StartZ=0 EndX=-2.75 EndY=-2.75 EndZ=0
    g2: LineSegment StartX=-2.75 StartY=-2.75 StartZ=0 EndX=-4.25 EndY=-2.75 EndZ=0
    g3: LineSegment StartX=-4.25 StartY=-2.75 StartZ=0 EndX=-4.25 EndY=-0.75 EndZ=0
    g4: LineSegment StartX=2.75 StartY=-0.75 StartZ=0 EndX=4.25 EndY=-0.75 EndZ=0
    g5: LineSegment StartX=4.25 StartY=-0.75 StartZ=0 EndX=4.25 EndY=-2.75 EndZ=0
    g6: LineSegment StartX=4.25 StartY=-2.75 StartZ=0 EndX=2.75 EndY=-2.75 EndZ=0
    g7: LineSegment StartX=2.75 StartY=-2.75 StartZ=0 EndX=2.75 EndY=-0.75 EndZ=0
    g8: LineSegment StartX=-4 StartY=-8 StartZ=0 EndX=-1.5 EndY=-8 EndZ=0
    g9: LineSegment StartX=-1.5 StartY=-8 StartZ=0 EndX=-1.5 EndY=-9.5 EndZ=0
    g10: LineSegment StartX=-1.5 StartY=-9.5 StartZ=0 EndX=-4 EndY=-9.5 EndZ=0
    g11: LineSegment StartX=-4 StartY=-9.5 StartZ=0 EndX=-4 EndY=-8 EndZ=0
    g12: LineSegment StartX=1.5 StartY=-8 StartZ=0 EndX=4 EndY=-8 EndZ=0
    g13: LineSegment StartX=4 StartY=-8 StartZ=0 EndX=4 EndY=-9.5 EndZ=0
    g14: LineSegment StartX=4 StartY=-9.5 StartZ=0 EndX=1.5 EndY=-9.5 EndZ=0
    g15: LineSegment StartX=1.5 StartY=-9.5 StartZ=0 EndX=1.5 EndY=-8 EndZ=0
  constraints (48):
    c: Coincident(g0,g1)
    c: Coincident(g1,g2)
    c: Coincident(g2,g3)
    c: Coincident(g3,g0)
    c: Horizontal(g0)
    c: Horizontal(g2)
    c: Vertical(g1)
    c: Vertical(g3)
    c: Distance(g0) = 1.5
    c: Distance(g3) = 2
    c: DistanceY(g0,g-1) = 0.75
    c: DistanceX(g0,g-1) = 2.75
    c: Coincident(g4,g5)
    c: Coincident(g5,g6)
    c: Coincident(g6,g7)
    c: Coincident(g7,g4)
    c: Horizontal(g4)
    c: Horizontal(g6)
    c: Vertical(g5)
    c: Vertical(g7)
    c: Distance(g4) = 1.5
    c: Distance(g7) = 2
    c: DistanceY(g4,g-1) = 0.75
    c: DistanceX(g-1,g4) = 2.75
    c: Coincident(g8,g9)
    c: Coincident(g9,g10)
    c: Coincident(g10,g11)
    c: Coincident(g11,g8)
    c: Horizontal(g8)
    c: Horizontal(g10)
    c: Vertical(g9)
    c: Vertical(g11)
    c: Coincident(g12,g13)
    c: Coincident(g13,g14)
    c: Coincident(g14,g15)
    c: Coincident(g15,g12)
    c: Horizontal(g12)
    c: Horizontal(g14)
    c: Vertical(g13)
    c: Vertical(g15)
    c: Distance(g10) = 2.5
    c: Distance(g14) = 2.5
    c: Distance(g9) = 1.5
    c: Distance(g15) = 1.5
    c: DistanceX(g8,g-1) = 1.5
    c: DistanceX(g-1,g12) = 1.5
    c: Horizontal(g12,g8)
    c: DistanceY(g8,g-1) = 8
FEATURE [PartDesign::Pocket] Pocket005
  BaseFeature = -> Pocket004
  Length = 5
  Length2 = 100
  Placement = pos=(0,0,0) rot=(0.57735,0.57735,0.57735;2.0944rad)
  Profile = -> Sketch014
  Type = 1
FEATURE [PartDesign::Body] Body002
  Group = -> [Sketch008,Pad001,Sketch009,Pocket003,Sketch010,Pocket004,Sketch011,Sketch012,Sketch013,Sketch014,Pocket005]
  Origin = -> Origin002
  Placement = pos=(12,-12,19) rot=(0.707107,0.707107,0;3.14159rad)
  Tip = -> Pocket005
FEATURE [Part::MultiFuse] Fusion
  Shapes = -> [Body001,Body002]
FEATURE [PartDesign::CoordinateSystem] LCS_0
  AttacherType = Attacher::AttachEngine3D
  MapMode = 2
  Support = -> [X_Axis]
FEATURE [PartDesign::CoordinateSystem] ScrewTop_LCS
  AttacherType = Attacher::AttachEngine3D
  AttachmentOffset = pos=(0,0,0) rot=(0,1,0;3.14159rad)
  MapMode = 45
  Placement = pos=(12,-12,14) rot=(0,0.707107,-0.707107;3.14159rad)
  Support = -> [Fusion]
FEATURE [PartDesign::CoordinateSystem] ScrewBottom_LCS
  AttacherType = Attacher::AttachEngine3D
  MapMode = 45
  Placement = pos=(-2e-15,1.47e-14,5) rot=(0.57735,0.57735,0.57735;2.0944rad)
  Support = -> [Pocket002]
FEATURE [App::Part] CenterSlider  label="Carriage_bottom-center"
  Group = -> [LCS_0,Body002,Body001,Fusion,ScrewTop_LCS,ScrewBottom_LCS]
  Origin = -> Origin
---- part MicroManipulator_Handle.FCStd = doc fcstd_dd35a5cda610 ----
FCSTD DOCUMENT  (FreeCAD 0.19R24344 (Git))
Label: MicroManipulator_Handle
License: All rights reserved
LicenseURL: http://en.wikipedia.org/wiki/All_rights_reserved
objects: Sketcher::SketchObject×1, PartDesign::Pad×1, PartDesign::CoordinateSystem×1, PartDesign::Body×1
note: 5 computed .brp shape members not serialized (recipe doc carries the construction recipe); baked Part::Feature solids carry a one-line shape summary decoded from their .brp

FEATURE [Sketcher::SketchObject] Sketch
  FullyConstrained = true
  MapMode = 5
  Support = -> [XY_Plane]
  sketch-geometry (31):
    g0: LineSegment StartX=2.77128 StartY=-1.6 StartZ=0 EndX=2.77128 EndY=1.6 EndZ=0
    g1: LineSegment StartX=2.77128 StartY=1.6 StartZ=0 EndX=0 EndY=3.2 EndZ=0
    g2: LineSegment StartX=0 StartY=3.2 StartZ=0 EndX=-2.77128 EndY=1.6 EndZ=0
    g3: LineSegment StartX=-2.77128 StartY=1.6 StartZ=0 EndX=-2.77128 EndY=-1.6 EndZ=0
    g4: LineSegment StartX=-2.77128 StartY=-1.6 StartZ=0 EndX=0 EndY=-3.2 EndZ=0
    g5: LineSegment StartX=0 StartY=-3.2 StartZ=0 EndX=2.77128 EndY=-1.6 EndZ=0
    g6: Circle CenterX=0 CenterY=0 CenterZ=0 NormalX=0 NormalY=0 NormalZ=1 AngleXU=0 Radius=3.2
    g7: LineSegment StartX=4.75043 StartY=4.4366 StartZ=0 EndX=3.3773 EndY=5.55373 EndZ=0
    g8: LineSegment StartX=3.3773 StartY=5.55373 StartZ=0 EndX=1.75368 EndY=6.25896 EndZ=0
    g9: LineSegment StartX=1.75368 StartY=6.25896 StartZ=0 EndX=0 EndY=6.5 EndZ=0
    g10: LineSegment StartX=0 StartY=6.5 StartZ=0 EndX=-1.75368 EndY=6.25896 EndZ=0
    g11: LineSegment StartX=-1.75368 StartY=6.25896 StartZ=0 EndX=-3.3773 EndY=5.55373 EndZ=0
    g12: LineSegment StartX=-3.3773 StartY=5.55373 StartZ=0 EndX=-4.75043 EndY=4.4366 EndZ=0
    g13: LineSegment StartX=-4.75043 StartY=4.4366 StartZ=0 EndX=-5.77125 EndY=2.99042 EndZ=0
    g14: LineSegment StartX=-5.77125 StartY=2.99042 StartZ=0 EndX=-6.36405 EndY=1.32246 EndZ=0
    g15: LineSegment StartX=-6.36405 StartY=1.32246 StartZ=0 EndX=-6.48485 EndY=-0.443576 EndZ=0
    g16: LineSegment StartX=-6.48485 StartY=-0.443576 StartZ=0 EndX=-6.1247 EndY=-2.17672 EndZ=0
    g17: LineSegment StartX=-6.1247 StartY=-2.17672 StartZ=0 EndX=-5.3103 EndY=-3.74842 EndZ=0
    g18: LineSegment StartX=-5.3103 StartY=-3.74842 StartZ=0 EndX=-4.10207 EndY=-5.04212 EndZ=0
    g19: LineSegment StartX=-4.10207 StartY=-5.04212 StartZ=0 EndX=-2.58961 EndY=-5.96187 EndZ=0
    g20: LineSegment StartX=-2.58961 StartY=-5.96187 StartZ=0 EndX=-0.885083 EndY=-6.43946 EndZ=0
    g21: LineSegment StartX=-0.885083 StartY=-6.43946 StartZ=0 EndX=0.885083 EndY=-6.43946 EndZ=0
    g22: LineSegment StartX=0.885083 StartY=-6.43946 StartZ=0 EndX=2.58961 EndY=-5.96187 EndZ=0
    g23: LineSegment StartX=2.58961 StartY=-5.96187 StartZ=0 EndX=4.10207 EndY=-5.04212 EndZ=0
    g24: LineSegment StartX=4.10207 StartY=-5.04212 StartZ=0 EndX=5.3103 EndY=-3.74842 EndZ=0
    g25: LineSegment StartX=5.3103 StartY=-3.74842 StartZ=0 EndX=6.1247 EndY=-2.17672 EndZ=0
    g26: LineSegment StartX=6.1247 StartY=-2.17672 StartZ=0 EndX=6.48485 EndY=-0.443576 EndZ=0
    g27: LineSegment StartX=6.48485 StartY=-0.443576 StartZ=0 EndX=6.36405 EndY=1.32246 EndZ=0
    g28: LineSegment StartX=6.36405 StartY=1.32246 StartZ=0 EndX=5.77125 EndY=2.99042 EndZ=0
    g29: LineSegment StartX=5.77125 StartY=2.99042 StartZ=0 EndX=4.75043 EndY=4.4366 EndZ=0
    g30: Circle CenterX=0 CenterY=0 CenterZ=0 NormalX=0 NormalY=0 NormalZ=1 AngleXU=0 Radius=6.5
  constraints (66):
    c: Coincident(g0,g1)
    c: Coincident(g1,g2)
    c: Coincident(g2,g3)
    c: Coincident(g3,g4)
    c: Coincident(g4,g5)
    c: Coincident(g5,g0)
    c: Equal(g0, g1-g5) x5
    c: PointOnObject(g0,g6)
    c: PointOnObject(g1,g6)
    c: PointOnObject(g2,g6)
    c: PointOnObject(g3,g6)
    c: PointOnObject(g4,g6)
    c: PointOnObject(g5,g6)
    c: Coincident(g6,g-1)
    c: Diameter(g6) = 6.4
    c: Coincident(g7,g8)
    c: Coincident(g8,g9)
    c: Coincident(g9,g10)
    c: Coincident(g10,g11)
    c: Coincident(g11,g12)
    c: Coincident(g12,g13)
    c: Coincident(g13,g14)
    c: Coincident(g14,g15)
    c: Coincident(g15,g16)
    c: Coincident(g16,g17)
    c: Coincident(g17,g18)
    c: Coincident(g18,g19)
    c: Coincident(g19,g20)
    c: Coincident(g20,g21)
    c: Coincident(g21,g22)
    c: Coincident(g22,g23)
    c: Coincident(g23,g24)
    c: Coincident(g24,g25)
    c: Coincident(g25,g26)
    c: Coincident(g26,g27)
    c: Coincident(g27,g28)
    c: Coincident(g28,g29)
    c: Coincident(g29,g7)
    c: Equal(g7, g8-g29) x22
    c: PointOnObject(g7,g30)
    c: PointOnObject(g8,g30)
    c: PointOnObject(g9,g30)
    c: PointOnObject(g10,g30)
    c: PointOnObject(g11,g30)
    c: PointOnObject(g12,g30)
    c: PointOnObject(g13,g30)
    c: PointOnObject(g14,g30)
    c: PointOnObject(g15,g30)
    c: PointOnObject(g16,g30)
    c: PointOnObject(g17,g30)
    c: PointOnObject(g18,g30)
    c: PointOnObject(g19,g30)
    c: PointOnObject(g20,g30)
    c: PointOnObject(g21,g30)
    c: PointOnObject(g22,g30)
    c: PointOnObject(g23,g30)
    c: PointOnObject(g24,g30)
    c: PointOnObject(g25,g30)
    c: PointOnObject(g26,g30)
    c: PointOnObject(g27,g30)
    c: PointOnObject(g28,g30)
    c: PointOnObject(g29,g30)
    c: Coincident(g30,g-1)
    c: Diameter(g30) = 13
    c: Vertical(g1,g-1)
    c: Vertical(g9,g-1)
FEATURE [PartDesign::Pad] Pad
  Direction = (1,1,1)
  Length = 25
  Length2 = 100
  Profile = -> Sketch
  Type = 0
FEATURE [PartDesign::CoordinateSystem] LCS_Handle
  AttacherType = Attacher::AttachEngine3D
  MapMode = 45
  Placement = pos=(0,-3e-16,0) rot=(0,0,1;0.523599rad)
  Support = -> [Pad]
FEATURE [PartDesign::Body] Body  label="Handle"
  Group = -> [Sketch,Pad,LCS_Handle]
  Origin = -> Origin
  Tip = -> Pad
---- part MicroManipulator_Rail_bottom.FCStd = doc fcstd_676833a55b43 ----
FCSTD DOCUMENT  (FreeCAD 0.19R24344 (Git))
Label: MicroManipulator_Rail_bottom
Comment: Bottom rail for the MicroManipulator. Additional material for stability and 4 mounting holes with imperial distance for assembly.
License: Creative Commons Attribution-NonCommercial-ShareAlike
LicenseURL: http://creativecommons.org/licenses/by-nc-sa/4.0/
objects: PartDesign::CoordinateSystem×6, Sketcher::SketchObject×5, PartDesign::Pad×3, PartDesign::Pocket×2, PartDesign::Body×1, Part::FeaturePython×1
note: 23 computed .brp shape members not serialized (recipe doc carries the construction recipe); baked Part::Feature solids carry a one-line shape summary decoded from their .brp

FEATURE [Sketcher::SketchObject] Sketch
  FullyConstrained = true
  MapMode = 5
  Placement = pos=(0,0,0) rot=(0.57735,0.57735,0.57735;2.0944rad)
  Support = -> [YZ_Plane]
  sketch-geometry (14):
    g0: LineSegment StartX=-5 StartY=8 StartZ=0 EndX=-5 EndY=9 EndZ=0
    g1: LineSegment StartX=5 StartY=9 StartZ=0 EndX=5 EndY=8 EndZ=0
    g2: LineSegment StartX=5 StartY=3 StartZ=0 EndX=5 EndY=-4e-16 EndZ=0
    g3: LineSegment StartX=5 StartY=-4e-16 StartZ=0 EndX=2.5 EndY=-4e-16 EndZ=0
    g4: LineSegment StartX=-2.5 StartY=0 StartZ=0 EndX=-5 EndY=0 EndZ=0
    g5: LineSegment StartX=-5 StartY=0 StartZ=0 EndX=-5 EndY=3 EndZ=0
    g6: ArcOfCircle CenterX=4e-16 CenterY=-1.44338 CenterZ=0 NormalX=0 NormalY=0 NormalZ=1 AngleXU=0 Radius=2.88675 StartAngle=0.523599 EndAngle=2.61799
    g7: ArcOfCircle CenterX=-6.44338 CenterY=5.5 CenterZ=0 NormalX=0 NormalY=0 NormalZ=1 AngleXU=0 Radius=2.88675 StartAngle=5.23599 EndAngle=7.33038
    g8: ArcOfCircle CenterX=6.44338 CenterY=5.5 CenterZ=0 NormalX=0 NormalY=0 NormalZ=1 AngleXU=0 Radius=2.88675 StartAngle=2.0944 EndAngle=4.18879
    g9: LineSegment StartX=-5 StartY=9 StartZ=0 EndX=-6 EndY=9 EndZ=0
    g10: LineSegment StartX=-6 StartY=9 StartZ=0 EndX=-9.6397 EndY=-1 EndZ=0
    g11: LineSegment StartX=-9.6397 StartY=-1 StartZ=0 EndX=9.6397 EndY=-1 EndZ=0
    g12: LineSegment StartX=9.6397 StartY=-1 StartZ=0 EndX=6 EndY=9 EndZ=0
    g13: LineSegment StartX=6 StartY=9 StartZ=0 EndX=5 EndY=9 EndZ=0
  constraints (44):
    c: Vertical(g0)
    c: Vertical(g1)
    c: Vertical(g2)
    c: Coincident(g3,g2)
    c: Horizontal(g3)
    c: Horizontal(g4)
    c: Coincident(g5,g4)
    c: Vertical(g5)
    c: Coincident(g6,g4)
    c: Coincident(g6,g3)
    c: Coincident(g7,g5)
    c: Coincident(g7,g0)
    c: Coincident(g8,g2)
    c: Coincident(g8,g1)
    c: Vertical(g0,g5)
    c: Vertical(g1,g2)
    c: Angle(g7) = 2.0944
    c: Angle(g8) = 2.0944
    c: Angle(g6) = 2.0944
    c: Distance(g4,g3) = 5
    c: Distance(g5,g0) = 5
    c: Distance(g1,g2) = 5
    c: Horizontal(g0,g1)
    c: Symmetric(g1,g0,g-2)
    c: PointOnObject(g2,g-1)
    c: Symmetric(g3,g4,g-2)
    c: Distance(g0,g4) = 9
    c: Distance(g5,g4) = 3
    c: Coincident(g9,g0)
    c: Horizontal(g9)
    c: Coincident(g10,g9)
    c: Vertical(g10)
    c: Coincident(g11,g10)
    c: Coincident(g12,g11)
    c: Vertical(g12)
    c: Coincident(g13,g12)
    c: Horizontal(g13)
    c: Distance(g9) = 1
    c: Distance(g13) = 1
    c: Coincident(g13,g1)
    c: DistanceY(g11,g2) = 1
    c: DistanceX(g4,g2) = 10
    c: Symmetric(g10,g11,g-2)
    c: Angle(g12) = 1.91986
FEATURE [PartDesign::Pad] Pad
  Direction = (1,1,1)
  Length = 40
  Length2 = 100
  Placement = pos=(0,0,0) rot=(0.57735,0.57735,0.57735;2.0944rad)
  Profile = -> Sketch
  Type = 0
FEATURE [Sketcher::SketchObject] Sketch001
  ExternalGeometry = -> [Pad]
  FullyConstrained = true
  MapMode = 5
  Placement = pos=(0,0,0) rot=(0.57735,0.57735,-0.57735;4.18879rad)
  Support = -> [Pad]
  sketch-geometry (5):
    g0: LineSegment StartX=-9.6397 StartY=1 StartZ=0 EndX=9.6397 EndY=1 EndZ=0
    g1: LineSegment StartX=9.6397 StartY=1 StartZ=0 EndX=6 EndY=-9 EndZ=0
    g2: LineSegment StartX=6 StartY=-9 StartZ=0 EndX=-6 EndY=-9 EndZ=0
    g3: LineSegment StartX=-6 StartY=-9 StartZ=0 EndX=-9.6397 EndY=1 EndZ=0
    g4: Circle CenterX=0 CenterY=-5 CenterZ=0 NormalX=0 NormalY=0 NormalZ=1 AngleXU=0 Radius=1.6
  constraints (11):
    c: Coincident(g0,g1)
    c: Coincident(g1,g2)
    c: Coincident(g2,g3)
    c: Coincident(g3,g0)
    c: Coincident(g0,g-3)
    c: Coincident(g1,g-4)
    c: PointOnObject(g4,g-2)
    c: Diameter(g4) = 3.2
    c: DistanceY(g4,g-1) = 5
    c: Coincident(g2,g-3)
    c: Coincident(g0,g-4)
FEATURE [PartDesign::Pad] Pad001
  BaseFeature = -> Pad
  Direction = (1,1,1)
  Length = 2
  Length2 = 100
  Placement = pos=(0,0,0) rot=(0.57735,0.57735,0.57735;2.0944rad)
  Profile = -> Sketch001
  Reversed = true
  Type = 0
FEATURE [Sketcher::SketchObject] Sketch002
  FullyConstrained = true
  MapMode = 5
  Placement = pos=(3e-16,-4e-16,-1) rot=(0.707107,0.707107,0;3.14159rad)
  Support = -> [Pad001]
  sketch-geometry (12):
    g0: Circle CenterX=-12.7 CenterY=32.4 CenterZ=0 NormalX=0 NormalY=0 NormalZ=1 AngleXU=0 Radius=3.15
    g1: Circle CenterX=12.7 CenterY=32.4 CenterZ=0 NormalX=0 NormalY=0 NormalZ=1 AngleXU=0 Radius=3.15
    g2: Circle CenterX=-12.7 CenterY=7 CenterZ=0 NormalX=0 NormalY=0 NormalZ=1 AngleXU=0 Radius=3.15
    g3: Circle CenterX=12.7 CenterY=7 CenterZ=0 NormalX=0 NormalY=0 NormalZ=1 AngleXU=0 Radius=3.15
    g4: LineSegment StartX=-16 StartY=40 StartZ=0 EndX=16 EndY=40 EndZ=0
    g5: LineSegment StartX=20 StartY=36 StartZ=0 EndX=20 EndY=4 EndZ=0
    g6: LineSegment StartX=16 StartY=0 StartZ=0 EndX=-16 EndY=0 EndZ=0
    g7: LineSegment StartX=-20 StartY=4 StartZ=0 EndX=-20 EndY=36 EndZ=0
    g8: ArcOfCircle CenterX=-16 CenterY=36 CenterZ=0 NormalX=0 NormalY=0 NormalZ=1 AngleXU=0 Radius=4 StartAngle=1.5708 EndAngle=3.14159
    g9: ArcOfCircle CenterX=-16 CenterY=4 CenterZ=0 NormalX=0 NormalY=0 NormalZ=1 AngleXU=0 Radius=4 StartAngle=3.14159 EndAngle=4.71239
    g10: ArcOfCircle CenterX=16 CenterY=4 CenterZ=0 NormalX=0 NormalY=0 NormalZ=1 AngleXU=0 Radius=4 StartAngle=4.71239 EndAngle=6.28319
    g11: ArcOfCircle CenterX=16 CenterY=36 CenterZ=0 NormalX=0 NormalY=0 NormalZ=1 AngleXU=0 Radius=4 StartAngle=-9e-16 EndAngle=1.5708
  constraints (30):
    c: Diameter(g2) = 6.3
    c: Equal(g2,g3)
    c: Equal(g3,g1)
    c: Equal(g1,g0)
    c: DistanceX(g0,g1) = 25.4
    c: DistanceY(g3,g1) = 25.4
    c: Vertical(g1,g3)
    c: Vertical(g0,g2)
    c: Horizontal(g1,g0)
    c: Symmetric(g2,g3,g-2)
    c: Horizontal(g4)
    c: Vertical(g5)
    c: Vertical(g7)
    c: Tangent(g4,g8) = 1.5708
    c: Tangent(g7,g8) = 1.5708
    c: Tangent(g7,g9) = 1.5708
    c: Tangent(g6,g9) = 1.5708
    c: Tangent(g6,g10) = 1.5708
    c: Tangent(g5,g10) = 1.5708
    c: Tangent(g5,g11) = 1.5708
    c: Tangent(g4,g11) = 1.5708
    c: DistanceY(g6,g4) = 40
    c: DistanceX(g7,g5) = 40
    c: Horizontal(g6)
    c: Symmetric(g5,g7,g-2)
    c: Diameter(g11) = 8
    c: Diameter(g9) = 8
    c: Diameter(g10) = 8
    c: DistanceY(g6,g2) = 7
    c: PointOnObject(g6,g-1)
FEATURE [PartDesign::Pad] Pad002
  BaseFeature = -> Pad001
  Direction = (1,1,1)
  Length = 3
  Length2 = 100
  Placement = pos=(0,0,0) rot=(0.57735,0.57735,0.57735;2.0944rad)
  Profile = -> Sketch002
  Type = 0
FEATURE [Sketcher::SketchObject] Sketch003
  ExternalGeometry = -> [Pad002]
  FullyConstrained = true
  MapMode = 5
  Placement = pos=(7e-16,-7e-16,-1) rot=(0,0,-1;1.5708rad)
  Support = -> [Pad002]
  sketch-geometry (4):
    g0: Circle CenterX=-12.7 CenterY=32.4 CenterZ=0 NormalX=0 NormalY=0 NormalZ=1 AngleXU=0 Radius=5
    g1: Circle CenterX=12.7 CenterY=32.4 CenterZ=0 NormalX=0 NormalY=0 NormalZ=1 AngleXU=0 Radius=5
    g2: Circle CenterX=12.7 CenterY=7 CenterZ=0 NormalX=0 NormalY=0 NormalZ=1 AngleXU=0 Radius=5
    g3: Circle CenterX=-12.7 CenterY=7 CenterZ=0 NormalX=0 NormalY=0 NormalZ=1 AngleXU=0 Radius=5
  constraints (8):
    c: Coincident(g0,g-5)
    c: Coincident(g1,g-4)
    c: Coincident(g2,g-6)
    c: Coincident(g3,g-3)
    c: Equal(g3,g0)
    c: Equal(g0,g1)
    c: Equal(g1,g2)
    c: Diameter(g3) = 10
FEATURE [PartDesign::Pocket] Pocket
  BaseFeature = -> Pad002
  Length = 5
  Length2 = 100
  Placement = pos=(0,0,0) rot=(0.57735,0.57735,0.57735;2.0944rad)
  Profile = -> Sketch003
  Reversed = true
  Type = 0
FEATURE [Sketcher::SketchObject] Sketch004
  ExternalGeometry = -> [Pocket]
  FullyConstrained = true
  MapMode = 5
  Placement = pos=(-2.2e-15,-5,1.1e-15) rot=(0.57735,0.57735,0.57735;4.18879rad)
  Support = -> [Pocket]
  sketch-geometry (4):
    g0: LineSegment StartX=9 StartY=2 StartZ=0 EndX=3 EndY=2 EndZ=0
    g1: LineSegment StartX=3 StartY=2 StartZ=0 EndX=3 EndY=7 EndZ=0
    g2: LineSegment StartX=3 StartY=7 StartZ=0 EndX=9 EndY=7 EndZ=0
    g3: LineSegment StartX=9 StartY=7 StartZ=0 EndX=9 EndY=2 EndZ=0
  constraints (11):
    c: Coincident(g0,g1)
    c: Coincident(g1,g2)
    c: Coincident(g2,g3)
    c: Coincident(g3,g0)
    c: Horizontal(g0)
    c: Horizontal(g2)
    c: Vertical(g1)
    c: Vertical(g3)
    c: Coincident(g0,g-3)
    c: Distance(g3) = 5
    c: Distance(g0) = 6
FEATURE [PartDesign::Pocket] Pocket001
  BaseFeature = -> Pocket
  Length = 34
  Length2 = 100
  Midplane = true
  Placement = pos=(0,0,0) rot=(0.57735,0.57735,0.57735;2.0944rad)
  Profile = -> Sketch004
  Type = 0
FEATURE [PartDesign::CoordinateSystem] Bottom_Cage_LCS  label="LCS_Screw"
  AttacherType = Attacher::AttachEngine3D
  MapMode = 45
  Placement = pos=(-1e-15,7.6e-15,5) rot=(0.57735,0.57735,0.57735;2.0944rad)
  Support = -> [Pocket001]
FEATURE [PartDesign::CoordinateSystem] Bottom_Mount_Edge
  AttacherType = Attacher::AttachEngine3D
  MapMode = 45
  Placement = pos=(32.4,12.7,-4) rot=(0,0,1;1.5708rad)
  Support = -> [Pocket001]
FEATURE [PartDesign::CoordinateSystem] LCS_Fasten_1
  AttacherType = Attacher::AttachEngine3D
  MapMode = 45
  Placement = pos=(32.4,12.9572,-1) rot=(0,0,1;1.5708rad)
  Support = -> [Pocket001]
FEATURE [PartDesign::CoordinateSystem] LCS_Fasten_2
  AttacherType = Attacher::AttachEngine3D
  MapMode = 45
  Placement = pos=(7,12.9572,-1) rot=(0,0,1;1.5708rad)
  Support = -> [Pocket001]
FEATURE [PartDesign::CoordinateSystem] LCS_Fasten_3
  AttacherType = Attacher::AttachEngine3D
  MapMode = 45
  Placement = pos=(7,-12.9572,-1) rot=(0,0,1;1.5708rad)
  Support = -> [Pocket001]
FEATURE [PartDesign::CoordinateSystem] LCS_Fasten_4
  AttacherType = Attacher::AttachEngine3D
  MapMode = 45
  Placement = pos=(32.4,-12.9572,-1) rot=(0,0,1;1.5708rad)
  Support = -> [Pocket001]
FEATURE [PartDesign::Body] Body  label="Rail_bottom"
  Group = -> [Pad,Sketch001,Pad001,Sketch002,Pad002,Sketch003,Pocket,Sketch004,Pocket001,Bottom_Cage_LCS,Bottom_Mount_Edge,LCS_Fasten_1,LCS_Fasten_2,LCS_Fasten_3,LCS_Fasten_4]
  Origin = -> Origin
  Tip = -> Pocket001
FEATURE [Part::FeaturePython] Screw  label="M6x12-Screw"  # Fasteners workbench fastener (typed FeaturePython)
  Placement = pos=(32.4,12.7,-1) rot=(0,0,1;0rad)
  baseObject = -> Body [Edge116]
  diameter = 8
  invert = true
  length = 0
  lengthCustom = 12
  matchOuter = true
  offset = 0
  thread = false
  type = 27
---- part MicroManipulator_Rail_center.FCStd = doc fcstd_d1af87669d46 ----
FCSTD DOCUMENT  (FreeCAD 0.19R24344 (Git))
Label: MicroManipulator_Rail_center
Comment: Center rail for the MicroManipulator. It is derived from the Rail, but has some additional material for stability and some mount points for top rail.
License: Creative Commons Attribution-NonCommercial-ShareAlike
LicenseURL: http://creativecommons.org/licenses/by-nc-sa/4.0/
objects: Sketcher::SketchObject×7, PartDesign::Pad×4, PartDesign::Pocket×3, PartDesign::CoordinateSystem×3, PartDesign::Body×1, App::Part×1
note: 25 computed .brp shape members not serialized (recipe doc carries the construction recipe); baked Part::Feature solids carry a one-line shape summary decoded from their .brp

FEATURE [Sketcher::SketchObject] Sketch
  FullyConstrained = true
  MapMode = 5
  Placement = pos=(0,0,0) rot=(0.57735,0.57735,0.57735;2.0944rad)
  Support = -> [YZ_Plane]
  sketch-geometry (14):
    g0: LineSegment StartX=-5 StartY=8 StartZ=0 EndX=-5 EndY=9 EndZ=0
    g1: LineSegment StartX=5 StartY=9 StartZ=0 EndX=5 EndY=8 EndZ=0
    g2: LineSegment StartX=5 StartY=3 StartZ=0 EndX=5 EndY=-1.5561e-12 EndZ=0
    g3: LineSegment StartX=5 StartY=-1.5561e-12 StartZ=0 EndX=2.5 EndY=-1.5561e-12 EndZ=0
    g4: LineSegment StartX=-2.5 StartY=-2.6472e-12 StartZ=0 EndX=-5 EndY=-2.6472e-12 EndZ=0
    g5: LineSegment StartX=-5 StartY=-2.6472e-12 StartZ=0 EndX=-5 EndY=3 EndZ=0
    g6: ArcOfCircle CenterX=7.111e-13 CenterY=-1.44338 CenterZ=0 NormalX=0 NormalY=0 NormalZ=1 AngleXU=0 Radius=2.88675 StartAngle=0.523599 EndAngle=2.61799
    g7: ArcOfCircle CenterX=-6.44338 CenterY=5.5 CenterZ=0 NormalX=0 NormalY=0 NormalZ=1 AngleXU=0 Radius=2.88675 StartAngle=5.23599 EndAngle=7.33038
    g8: ArcOfCircle CenterX=6.44338 CenterY=5.5 CenterZ=0 NormalX=0 NormalY=0 NormalZ=1 AngleXU=0 Radius=2.88675 StartAngle=2.0944 EndAngle=4.18879
    g9: LineSegment StartX=-5 StartY=9 StartZ=0 EndX=-6 EndY=9 EndZ=0
    g10: LineSegment StartX=-6 StartY=9 StartZ=0 EndX=-6 EndY=-2 EndZ=0
    g11: LineSegment StartX=-6 StartY=-2 StartZ=0 EndX=6 EndY=-2 EndZ=0
    g12: LineSegment StartX=6 StartY=-2 StartZ=0 EndX=6 EndY=9 EndZ=0
    g13: LineSegment StartX=6 StartY=9 StartZ=0 EndX=5 EndY=9 EndZ=0
  constraints (43):
    c: Vertical(g0)
    c: Vertical(g1)
    c: Vertical(g2)
    c: Coincident(g3,g2)
    c: Horizontal(g3)
    c: Horizontal(g4)
    c: Coincident(g5,g4)
    c: Vertical(g5)
    c: Coincident(g6,g4)
    c: Coincident(g6,g3)
    c: Coincident(g7,g5)
    c: Coincident(g7,g0)
    c: Coincident(g8,g2)
    c: Coincident(g8,g1)
    c: Vertical(g0,g5)
    c: Vertical(g1,g2)
    c: Angle(g7) = 2.0944
    c: Angle(g8) = 2.0944
    c: Angle(g6) = 2.0944
    c: Distance(g4,g3) = 5
    c: Distance(g5,g0) = 5
    c: Distance(g1,g2) = 5
    c: Horizontal(g0,g1)
    c: Symmetric(g1,g0,g-2)
    c: PointOnObject(g2,g-1)
    c: Symmetric(g3,g4,g-2)
    c: Distance(g0,g4) = 9
    c: Distance(g5,g4) = 3
    c: Coincident(g9,g0)
    c: Horizontal(g9)
    c: Coincident(g10,g9)
    c: Vertical(g10)
    c: Coincident(g11,g10)
    c: Horizontal(g11)
    c: Coincident(g12,g11)
    c: Vertical(g12)
    c: Coincident(g13,g12)
    c: Horizontal(g13)
    c: Distance(g9) = 1
    c: Distance(g13) = 1
    c: Coincident(g13,g1)
    c: DistanceY(g11,g2) = 2
    c: DistanceX(g4,g2) = 10
FEATURE [PartDesign::Pad] Pad
  Direction = (1,1,1)
  Length = 40
  Length2 = 100
  Placement = pos=(0,0,0) rot=(0.57735,0.57735,0.57735;2.0944rad)
  Profile = -> Sketch
  Type = 0
FEATURE [Sketcher::SketchObject] Sketch001
  ExternalGeometry = -> [Pad]
  FullyConstrained = true
  MapMode = 5
  Placement = pos=(0,0,0) rot=(0.57735,0.57735,-0.57735;4.18879rad)
  Support = -> [Pad]
  sketch-geometry (5):
    g0: LineSegment StartX=-6 StartY=2 StartZ=0 EndX=6 EndY=2 EndZ=0
    g1: LineSegment StartX=6 StartY=2 StartZ=0 EndX=6 EndY=-9 EndZ=0
    g2: LineSegment StartX=6 StartY=-9 StartZ=0 EndX=-6 EndY=-9 EndZ=0
    g3: LineSegment StartX=-6 StartY=-9 StartZ=0 EndX=-6 EndY=2 EndZ=0
    g4: Circle CenterX=0 CenterY=-5 CenterZ=0 NormalX=0 NormalY=0 NormalZ=1 AngleXU=0 Radius=1.6
  constraints (13):
    c: Coincident(g0,g1)
    c: Coincident(g1,g2)
    c: Coincident(g2,g3)
    c: Coincident(g3,g0)
    c: Horizontal(g0)
    c: Horizontal(g2)
    c: Vertical(g1)
    c: Vertical(g3)
    c: Coincident(g0,g-3)
    c: Coincident(g1,g-4)
    c: PointOnObject(g4,g-2)
    c: Diameter(g4) = 3.2
    c: DistanceY(g4,g-1) = 5
FEATURE [PartDesign::Pad] Pad001
  BaseFeature = -> Pad
  Direction = (1,1,1)
  Length = 2
  Length2 = 100
  Placement = pos=(0,0,0) rot=(0.57735,0.57735,0.57735;2.0944rad)
  Profile = -> Sketch001
  Type = 0
FEATURE [Sketcher::SketchObject] Sketch002
  FullyConstrained = true
  MapMode = 5
  Placement = pos=(6e-16,-9e-16,-2) rot=(0.707107,0.707107,0;3.14159rad)
  Support = -> [Pad001]
  sketch-geometry (12):
    g0: Circle CenterX=-10 CenterY=25 CenterZ=0 NormalX=0 NormalY=0 NormalZ=1 AngleXU=0 Radius=1.6
    g1: Circle CenterX=-10 CenterY=15 CenterZ=0 NormalX=0 NormalY=0 NormalZ=1 AngleXU=0 Radius=1.6
    g2: Circle CenterX=10 CenterY=15 CenterZ=0 NormalX=0 NormalY=0 NormalZ=1 AngleXU=0 Radius=1.6
    g3: Circle CenterX=10 CenterY=25 CenterZ=0 NormalX=0 NormalY=0 NormalZ=1 AngleXU=0 Radius=1.6
    g4: LineSegment StartX=-10 StartY=29 StartZ=0 EndX=10 EndY=29 EndZ=0
    g5: LineSegment StartX=14 StartY=25 StartZ=0 EndX=14 EndY=15 EndZ=0
    g6: LineSegment StartX=10 StartY=11 StartZ=0 EndX=-10 EndY=11 EndZ=0
    g7: LineSegment StartX=-14 StartY=15 StartZ=0 EndX=-14 EndY=25 EndZ=0
    g8: ArcOfCircle CenterX=-10 CenterY=25 CenterZ=0 NormalX=0 NormalY=0 NormalZ=1 AngleXU=0 Radius=4 StartAngle=1.5708 EndAngle=3.14159
    g9: ArcOfCircle CenterX=-10 CenterY=15 CenterZ=0 NormalX=0 NormalY=0 NormalZ=1 AngleXU=0 Radius=4 StartAngle=3.14159 EndAngle=4.71239
    g10: ArcOfCircle CenterX=10 CenterY=15 CenterZ=0 NormalX=0 NormalY=0 NormalZ=1 AngleXU=0 Radius=4 StartAngle=4.71239 EndAngle=6.28319
    g11: ArcOfCircle CenterX=10 CenterY=25 CenterZ=0 NormalX=0 NormalY=0 NormalZ=1 AngleXU=0 Radius=4 StartAngle=0 EndAngle=1.5708
  constraints (27):
    c: Equal(g1,g0)
    c: Equal(g0,g3)
    c: Equal(g3,g2)
    c: Diameter(g0) = 3.2
    c: Vertical(g3,g2)
    c: Symmetric(g0,g3,g-2)
    c: Symmetric(g1,g2,g-2)
    c: DistanceY(g2,g3) = 10
    c: DistanceX(g0,g3) = 20
    c: Horizontal(g4)
    c: Horizontal(g6)
    c: Vertical(g5)
    c: Vertical(g7)
    c: Tangent(g4,g8) = 1.5708
    c: Tangent(g7,g8) = 1.5708
    c: Tangent(g7,g9) = 1.5708
    c: Tangent(g6,g9) = 1.5708
    c: Tangent(g6,g10) = 1.5708
    c: Tangent(g5,g10) = 1.5708
    c: Tangent(g5,g11) = 1.5708
    c: Tangent(g4,g11) = 1.5708
    c: Diameter(g11) = 8
    c: Diameter(g10) = 8
    c: Coincident(g8,g0)
    c: Coincident(g9,g1)
    c: Coincident(g10,g2)
    c: DistanceY(g-1,g2) = 15
FEATURE [PartDesign::Pad] Pad002
  BaseFeature = -> Pad001
  Direction = (1,1,1)
  Length = 2
  Length2 = 100
  Midplane = true
  Placement = pos=(0,0,0) rot=(0.57735,0.57735,0.57735;2.0944rad)
  Profile = -> Sketch002
  Type = 0
FEATURE [Sketcher::SketchObject] Sketch003
  ExternalGeometry = -> [Pad002]
  FullyConstrained = true
  MapMode = 5
  Placement = pos=(-2.6e-15,-6,1.3e-15) rot=(-0.57735,-0.57735,0.57735;4.18879rad)
  Support = -> [Pad002]
  sketch-geometry (5):
    g0: LineSegment StartX=-9 StartY=0.4 StartZ=0 EndX=-4.5 EndY=0.4 EndZ=0
    g1: LineSegment StartX=-2.5 StartY=2.4 StartZ=0 EndX=-2.5 EndY=5.4 EndZ=0
    g2: LineSegment StartX=-2.5 StartY=5.4 StartZ=0 EndX=-9 EndY=5.4 EndZ=0
    g3: LineSegment StartX=-9 StartY=5.4 StartZ=0 EndX=-9 EndY=0.4 EndZ=0
    g4: ArcOfCircle CenterX=-4.5 CenterY=2.4 CenterZ=0 NormalX=0 NormalY=0 NormalZ=1 AngleXU=0 Radius=2 StartAngle=4.71239 EndAngle=6.28319
  constraints (14):
    c: Coincident(g1,g2)
    c: Coincident(g2,g3)
    c: Coincident(g3,g0)
    c: Horizontal(g0)
    c: Horizontal(g2)
    c: Vertical(g1)
    c: Vertical(g3)
    c: Distance(g3) = 5
    c: DistanceY(g-1,g0) = 0.4
    c: PointOnObject(g2,g-3)
    c: Tangent(g0,g4) = -1.5708
    c: Tangent(g1,g4) = -1.5708
    c: Radius(g4) = 2
    c: DistanceX(g1,g-1) = 2.5
FEATURE [PartDesign::Pocket] Pocket
  BaseFeature = -> Pad002
  Length = 5
  Length2 = 100
  Placement = pos=(0,0,0) rot=(0.57735,0.57735,0.57735;2.0944rad)
  Profile = -> Sketch003
  Type = 1
FEATURE [Sketcher::SketchObject] Sketch004
  ExternalGeometry = -> [Pocket]
  FullyConstrained = true
  MapMode = 5
  Placement = pos=(40,-8.8e-15,8.8e-15) rot=(0.57735,0.57735,0.57735;2.0944rad)
  Support = -> [Pocket]
  sketch-geometry (6):
    g0: LineSegment StartX=-6 StartY=9 StartZ=0 EndX=-10 EndY=-2 EndZ=0
    g1: LineSegment StartX=-10 StartY=-2 StartZ=0 EndX=10 EndY=-2 EndZ=0
    g2: LineSegment StartX=10 StartY=-2 StartZ=0 EndX=6 EndY=9 EndZ=0
    g3: LineSegment StartX=-6 StartY=9 StartZ=0 EndX=-6 EndY=-1 EndZ=0
    g4: LineSegment StartX=-6 StartY=-1 StartZ=0 EndX=6 EndY=-1 EndZ=0
    g5: LineSegment StartX=6 StartY=-1 StartZ=0 EndX=6 EndY=9 EndZ=0
  constraints (15):
    c: Coincident(g0,g-5)
    c: Coincident(g1,g0)
    c: Coincident(g2,g1)
    c: Coincident(g2,g-4)
    c: PointOnObject(g-4,g1)
    c: Symmetric(g1,g0,g-2)
    c: DistanceX(g-1,g1) = 10
    c: Coincident(g3,g0)
    c: PointOnObject(g3,g-5)
    c: Coincident(g4,g3)
    c: PointOnObject(g4,g-4)
    c: Horizontal(g4)
    c: Coincident(g5,g4)
    c: Coincident(g5,g2)
    c: DistanceY(g1,g4) = 1
FEATURE [PartDesign::Pad] Pad003
  BaseFeature = -> Pocket
  Direction = (1,1,1)
  Length = 34
  Length2 = 100
  Placement = pos=(0,0,0) rot=(0.57735,0.57735,0.57735;2.0944rad)
  Profile = -> Sketch004
  Reversed = true
  Type = 0
FEATURE [Sketcher::SketchObject] Sketch005
  ExternalGeometry = -> [Pad003]
  FullyConstrained = true
  MapMode = 5
  Placement = pos=(7e-16,-7e-16,-1) rot=(0,0,-1;1.5708rad)
  Support = -> [Pad003]
  sketch-geometry (4):
    g0: Circle CenterX=-10 CenterY=25 CenterZ=0 NormalX=0 NormalY=0 NormalZ=1 AngleXU=0 Radius=3
    g1: Circle CenterX=10 CenterY=25 CenterZ=0 NormalX=0 NormalY=0 NormalZ=1 AngleXU=0 Radius=3
    g2: Circle CenterX=10 CenterY=15 CenterZ=0 NormalX=0 NormalY=0 NormalZ=1 AngleXU=0 Radius=3
    g3: Circle CenterX=-10 CenterY=15 CenterZ=0 NormalX=0 NormalY=0 NormalZ=1 AngleXU=0 Radius=3
  constraints (8):
    c: Coincident(g0,g-3)
    c: Coincident(g1,g-4)
    c: Coincident(g2,g-5)
    c: Coincident(g3,g-6)
    c: Equal(g3,g0)
    c: Equal(g0,g1)
    c: Equal(g1,g2)
    c: Diameter(g3) = 6
FEATURE [PartDesign::Pocket] Pocket001
  BaseFeature = -> Pad003
  Length = 11
  Length2 = 100
  Placement = pos=(0,0,0) rot=(0.57735,0.57735,0.57735;2.0944rad)
  Profile = -> Sketch005
  Reversed = true
  Type = 0
FEATURE [Sketcher::SketchObject] Sketch006
  ExternalGeometry = -> [Pocket001]
  FullyConstrained = true
  MapMode = 5
  Placement = pos=(7e-16,-7e-16,-1) rot=(0,0,-1;1.5708rad)
  Support = -> [Pocket001]
  sketch-geometry (4):
    g0: Circle CenterX=-10 CenterY=25 CenterZ=0 NormalX=0 NormalY=0 NormalZ=1 AngleXU=0 Radius=1.55
    g1: Circle CenterX=-10 CenterY=15 CenterZ=0 NormalX=0 NormalY=0 NormalZ=1 AngleXU=0 Radius=1.55
    g2: Circle CenterX=10 CenterY=25 CenterZ=0 NormalX=0 NormalY=0 NormalZ=1 AngleXU=0 Radius=1.55
    g3: Circle CenterX=10 CenterY=15 CenterZ=0 NormalX=0 NormalY=0 NormalZ=1 AngleXU=0 Radius=1.55
  constraints (8):
    c: Coincident(g0,g-3)
    c: Coincident(g1,g-4)
    c: Coincident(g2,g-5)
    c: Coincident(g3,g-6)
    c: Equal(g3,g2)
    c: Equal(g2,g0)
    c: Equal(g0,g1)
    c: Diameter(g2) = 3.1
FEATURE [PartDesign::Pocket] Pocket002
  BaseFeature = -> Pocket001
  Length = 5
  Length2 = 100
  Placement = pos=(0,0,0) rot=(0.57735,0.57735,0.57735;2.0944rad)
  Profile = -> Sketch006
  Type = 0
FEATURE [PartDesign::Body] Body
  Group = -> [Pad,Sketch001,Pad001,Sketch002,Pad002,Sketch003,Pocket,Sketch004,Pad003,Sketch005,Pocket001,Sketch006,Pocket002]
  Origin = -> Origin
  Tip = -> Pocket002
FEATURE [PartDesign::CoordinateSystem] LCS_0
  AttacherType = Attacher::AttachEngine3D
  MapMode = 2
  Support = -> [X_Axis001]
FEATURE [PartDesign::CoordinateSystem] Screw_LCS
  AttacherType = Attacher::AttachEngine3D
  MapMode = 45
  Placement = pos=(-2,8.6e-15,5) rot=(0.57735,0.57735,0.57735;2.0944rad)
  Support = -> [Pocket002]
FEATURE [PartDesign::CoordinateSystem] Top_Mount_LCS
  AttacherType = Attacher::AttachEngine3D
  AttachmentOffset = pos=(0,0,0) rot=(0,1,0;3.14159rad)
  MapMode = 45
  Placement = pos=(25,-10,-3) rot=(-0.707109,0.707105,0;3.14159rad)
  Support = -> [Pocket002]
FEATURE [App::Part] CenterCage  label="Rail_center"
  Group = -> [LCS_0,Body,Screw_LCS,Top_Mount_LCS]
  Origin = -> Origin001
---- part MicroManipulator_Rail_top.FCStd = doc fcstd_5499ba404284 ----
FCSTD DOCUMENT  (FreeCAD 0.19R24344 (Git))
Label: MicroManipulator_Rail_top
Comment: Top rail for the MicroManipulator. Still a bit flimpsy, might need additional material for stability.
License: Creative Commons Attribution-NonCommercial-ShareAlike
LicenseURL: http://creativecommons.org/licenses/by-nc-sa/4.0/
objects: PartDesign::CoordinateSystem×7, Sketcher::SketchObject×4, PartDesign::Pad×3, PartDesign::Pocket×1, PartDesign::Body×1, App::Part×1
note: 20 computed .brp shape members not serialized (recipe doc carries the construction recipe); baked Part::Feature solids carry a one-line shape summary decoded from their .brp

FEATURE [Sketcher::SketchObject] Sketch
  FullyConstrained = true
  MapMode = 5
  Placement = pos=(0,0,0) rot=(0.57735,0.57735,0.57735;2.0944rad)
  Support = -> [YZ_Plane]
  sketch-geometry (14):
    g0: LineSegment StartX=-5 StartY=8 StartZ=0 EndX=-5 EndY=9 EndZ=0
    g1: LineSegment StartX=5 StartY=9 StartZ=0 EndX=5 EndY=8 EndZ=0
    g2: LineSegment StartX=5 StartY=3 StartZ=0 EndX=5 EndY=-4e-16 EndZ=0
    g3: LineSegment StartX=5 StartY=-4e-16 StartZ=0 EndX=2.5 EndY=-4e-16 EndZ=0
    g4: LineSegment StartX=-2.5 StartY=-2e-16 StartZ=0 EndX=-5 EndY=-2e-16 EndZ=0
    g5: LineSegment StartX=-5 StartY=-2e-16 StartZ=0 EndX=-5 EndY=3 EndZ=0
    g6: ArcOfCircle CenterX=1e-16 CenterY=-1.44338 CenterZ=0 NormalX=0 NormalY=0 NormalZ=1 AngleXU=0 Radius=2.88675 StartAngle=0.523599 EndAngle=2.61799
    g7: ArcOfCircle CenterX=-6.44338 CenterY=5.5 CenterZ=0 NormalX=0 NormalY=0 NormalZ=1 AngleXU=0 Radius=2.88675 StartAngle=5.23599 EndAngle=7.33038
    g8: ArcOfCircle CenterX=6.44338 CenterY=5.5 CenterZ=0 NormalX=0 NormalY=0 NormalZ=1 AngleXU=0 Radius=2.88675 StartAngle=2.0944 EndAngle=4.18879
    g9: LineSegment StartX=-5 StartY=9 StartZ=0 EndX=-6 EndY=9 EndZ=0
    g10: LineSegment StartX=-6 StartY=9 StartZ=0 EndX=-6 EndY=-1 EndZ=0
    g11: LineSegment StartX=-6 StartY=-1 StartZ=0 EndX=6 EndY=-1 EndZ=0
    g12: LineSegment StartX=6 StartY=-1 StartZ=0 EndX=6 EndY=9 EndZ=0
    g13: LineSegment StartX=6 StartY=9 StartZ=0 EndX=5 EndY=9 EndZ=0
  constraints (43):
    c: Vertical(g0)
    c: Vertical(g1)
    c: Vertical(g2)
    c: Coincident(g3,g2)
    c: Horizontal(g3)
    c: Horizontal(g4)
    c: Coincident(g5,g4)
    c: Vertical(g5)
    c: Coincident(g6,g4)
    c: Coincident(g6,g3)
    c: Coincident(g7,g5)
    c: Coincident(g7,g0)
    c: Coincident(g8,g2)
    c: Coincident(g8,g1)
    c: Vertical(g0,g5)
    c: Vertical(g1,g2)
    c: Angle(g7) = 2.0944
    c: Angle(g8) = 2.0944
    c: Angle(g6) = 2.0944
    c: Distance(g4,g3) = 5
    c: Distance(g5,g0) = 5
    c: Distance(g1,g2) = 5
    c: Horizontal(g0,g1)
    c: Symmetric(g1,g0,g-2)
    c: PointOnObject(g2,g-1)
    c: Symmetric(g3,g4,g-2)
    c: Distance(g0,g4) = 9
    c: Distance(g5,g4) = 3
    c: Coincident(g9,g0)
    c: Horizontal(g9)
    c: Coincident(g10,g9)
    c: Vertical(g10)
    c: Coincident(g11,g10)
    c: Horizontal(g11)
    c: Coincident(g12,g11)
    c: Vertical(g12)
    c: Coincident(g13,g12)
    c: Horizontal(g13)
    c: Distance(g9) = 1
    c: Distance(g13) = 1
    c: Coincident(g13,g1)
    c: DistanceY(g11,g2) = 1
    c: DistanceX(g4,g2) = 10
FEATURE [PartDesign::Pad] Pad
  Direction = (1,1,1)
  Length = 40
  Length2 = 100
  Placement = pos=(0,0,0) rot=(0.57735,0.57735,0.57735;2.0944rad)
  Profile = -> Sketch
  Type = 0
FEATURE [Sketcher::SketchObject] Sketch001
  ExternalGeometry = -> [Pad]
  FullyConstrained = true
  MapMode = 5
  Placement = pos=(0,0,0) rot=(0.57735,0.57735,-0.57735;4.18879rad)
  Support = -> [Pad]
  sketch-geometry (5):
    g0: LineSegment StartX=-6 StartY=1 StartZ=0 EndX=6 EndY=1 EndZ=0
    g1: LineSegment StartX=6 StartY=1 StartZ=0 EndX=6 EndY=-9 EndZ=0
    g2: LineSegment StartX=6 StartY=-9 StartZ=0 EndX=-6 EndY=-9 EndZ=0
    g3: LineSegment StartX=-6 StartY=-9 StartZ=0 EndX=-6 EndY=1 EndZ=0
    g4: Circle CenterX=0 CenterY=-5 CenterZ=0 NormalX=0 NormalY=0 NormalZ=1 AngleXU=0 Radius=1.6
  constraints (13):
    c: Coincident(g0,g1)
    c: Coincident(g1,g2)
    c: Coincident(g2,g3)
    c: Coincident(g3,g0)
    c: Horizontal(g0)
    c: Horizontal(g2)
    c: Vertical(g1)
    c: Vertical(g3)
    c: Coincident(g0,g-3)
    c: Coincident(g1,g-4)
    c: PointOnObject(g4,g-2)
    c: Diameter(g4) = 3.2
    c: DistanceY(g4,g-1) = 5
FEATURE [PartDesign::Pad] Pad001
  BaseFeature = -> Pad
  Direction = (1,1,1)
  Length = 2
  Length2 = 100
  Placement = pos=(0,0,0) rot=(0.57735,0.57735,0.57735;2.0944rad)
  Profile = -> Sketch001
  Type = 0
FEATURE [Sketcher::SketchObject] Sketch002
  ExternalGeometry = -> [Pad001]
  FullyConstrained = true
  MapMode = 5
  Placement = pos=(40,-8.8e-15,8.8e-15) rot=(0.57735,0.57735,0.57735;2.0944rad)
  Support = -> [Pad001]
  sketch-geometry (14):
    g0: Circle CenterX=-10 CenterY=9 CenterZ=0 NormalX=0 NormalY=0 NormalZ=1 AngleXU=0 Radius=1.55
    g1: Circle CenterX=10 CenterY=9 CenterZ=0 NormalX=0 NormalY=0 NormalZ=1 AngleXU=0 Radius=1.55
    g2: Circle CenterX=10 CenterY=-1 CenterZ=0 NormalX=0 NormalY=0 NormalZ=1 AngleXU=0 Radius=1.55
    g3: Circle CenterX=-10 CenterY=-1 CenterZ=0 NormalX=0 NormalY=0 NormalZ=1 AngleXU=0 Radius=1.55
    g4: ArcOfCircle CenterX=-10 CenterY=9 CenterZ=0 NormalX=0 NormalY=0 NormalZ=1 AngleXU=0 Radius=4 StartAngle=4e-16 EndAngle=3.14159
    g5: ArcOfCircle CenterX=-10 CenterY=-1 CenterZ=0 NormalX=0 NormalY=0 NormalZ=1 AngleXU=0 Radius=4 StartAngle=3.14159 EndAngle=4.71239
    g6: LineSegment StartX=-14 StartY=9 StartZ=0 EndX=-14 EndY=-1 EndZ=0
    g7: ArcOfCircle CenterX=10 CenterY=-1 CenterZ=0 NormalX=0 NormalY=0 NormalZ=1 AngleXU=0 Radius=4 StartAngle=4.71239 EndAngle=6.28319
    g8: ArcOfCircle CenterX=10 CenterY=9 CenterZ=0 NormalX=0 NormalY=0 NormalZ=1 AngleXU=0 Radius=4 StartAngle=1e-16 EndAngle=3.14159
    g9: LineSegment StartX=14 StartY=9 StartZ=0 EndX=14 EndY=-1 EndZ=0
    g10: LineSegment StartX=10 StartY=-5 StartZ=0 EndX=-10 EndY=-5 EndZ=0
    g11: LineSegment StartX=-6 StartY=9 StartZ=0 EndX=-5 EndY=1.8e-15 EndZ=0
    g12: LineSegment StartX=-5 StartY=1.8e-15 StartZ=0 EndX=5 EndY=1.8e-15 EndZ=0
    g13: LineSegment StartX=5 StartY=1.8e-15 StartZ=0 EndX=6 EndY=9 EndZ=0
  constraints (31):
    c: Diameter(g3) = 3.1
    c: Equal(g3,g0)
    c: Equal(g0,g1)
    c: Equal(g1,g2)
    c: DistanceX(g0,g1) = 20
    c: DistanceY(g3,g0) = 10
    c: Vertical(g0,g3)
    c: Vertical(g1,g2)
    c: Horizontal(g1,g0)
    c: DistanceY(g2,g-1) = 1
    c: Symmetric(g2,g3,g-2)
    c: Coincident(g4,g-3)
    c: Coincident(g0,g4)
    c: Vertical(g6)
    c: Tangent(g6,g4) = -1.5708
    c: Tangent(g6,g5) = -1.5708
    c: Coincident(g5,g3)
    c: Coincident(g8,g-4)
    c: Coincident(g8,g1)
    c: Coincident(g7,g2)
    c: Tangent(g10,g5) = 1.5708
    c: Tangent(g10,g7) = 1.5708
    c: Tangent(g9,g7) = 1.5708
    c: Tangent(g9,g8) = 1.5708
    c: Vertical(g9)
    c: Coincident(g11,g4)
    c: Coincident(g11,g-6)
    c: Coincident(g12,g11)
    c: Coincident(g12,g-5)
    c: Coincident(g13,g12)
    c: Coincident(g13,g8)
FEATURE [PartDesign::Pad] Pad002
  BaseFeature = -> Pad001
  Direction = (1,1,1)
  Length = 2
  Length2 = 100
  Placement = pos=(0,0,0) rot=(0.57735,0.57735,0.57735;2.0944rad)
  Profile = -> Sketch002
  Reversed = true
  Type = 0
FEATURE [Sketcher::SketchObject] Sketch003
  ExternalGeometry = -> [Pad002]
  FullyConstrained = true
  MapMode = 5
  Placement = pos=(-2.6e-15,-6,1.3e-15) rot=(-0.57735,-0.57735,0.57735;4.18879rad)
  Support = -> [Pad002]
  sketch-geometry (5):
    g0: LineSegment StartX=-9 StartY=0.4 StartZ=0 EndX=-4.5 EndY=0.4 EndZ=0
    g1: LineSegment StartX=-2.5 StartY=2.4 StartZ=0 EndX=-2.5 EndY=5.4 EndZ=0
    g2: LineSegment StartX=-2.5 StartY=5.4 StartZ=0 EndX=-9 EndY=5.4 EndZ=0
    g3: LineSegment StartX=-9 StartY=5.4 StartZ=0 EndX=-9 EndY=0.4 EndZ=0
    g4: ArcOfCircle CenterX=-4.5 CenterY=2.4 CenterZ=0 NormalX=0 NormalY=0 NormalZ=1 AngleXU=0 Radius=2 StartAngle=4.71239 EndAngle=6.28319
  constraints (14):
    c: Coincident(g1,g2)
    c: Coincident(g2,g3)
    c: Coincident(g3,g0)
    c: Horizontal(g0)
    c: Horizontal(g2)
    c: Vertical(g1)
    c: Vertical(g3)
    c: PointOnObject(g0,g-3)
    c: DistanceY(g-1,g0) = 0.4
    c: Distance(g3) = 5
    c: Tangent(g0,g4) = -1.5708
    c: Tangent(g1,g4) = -1.5708
    c: Radius(g4) = 2
    c: DistanceX(g1,g-1) = 2.5
FEATURE [PartDesign::Pocket] Pocket
  BaseFeature = -> Pad002
  Length = 5
  Length2 = 100
  Placement = pos=(0,0,0) rot=(0.57735,0.57735,0.57735;2.0944rad)
  Profile = -> Sketch003
  Type = 0
FEATURE [PartDesign::Body] Body
  Group = -> [Pad,Sketch001,Pad001,Sketch002,Pad002,Sketch003,Pocket]
  Origin = -> Origin
  Tip = -> Pocket
FEATURE [PartDesign::CoordinateSystem] LCS_0
  AttacherType = Attacher::AttachEngine3D
  MapMode = 2
  Support = -> [X_Axis001]
FEATURE [PartDesign::CoordinateSystem] Screw_LCS
  AttacherType = Attacher::AttachEngine3D
  MapMode = 45
  Placement = pos=(-2,9.6e-15,5) rot=(0.57735,0.57735,0.57735;2.0944rad)
  Support = -> [Pocket]
FEATURE [PartDesign::CoordinateSystem] MountPoint_LCS
  AttacherType = Attacher::AttachEngine3D
  AttachmentOffset = pos=(0,0,0) rot=(0,1,0;3.14159rad)
  MapMode = 45
  Placement = pos=(40,10,9) rot=(-0.57735,0.57735,0.57735;4.18879rad)
  Support = -> [Pocket]
FEATURE [PartDesign::CoordinateSystem] LCS_Fasten_1
  AttacherType = Attacher::AttachEngine3D
  MapMode = 11
  Placement = pos=(38,-10,9) rot=(0.707107,0,0.707107;3.14159rad)
  Support = -> [Pocket]
FEATURE [PartDesign::CoordinateSystem] LCS_Fasten_2
  AttacherType = Attacher::AttachEngine3D
  MapMode = 11
  Placement = pos=(38,-10,-1) rot=(0.707107,0,0.707107;3.14159rad)
  Support = -> [Pocket]
FEATURE [PartDesign::CoordinateSystem] LCS_Fasten_3
  AttacherType = Attacher::AttachEngine3D
  MapMode = 11
  Placement = pos=(38,10,9) rot=(0.707107,0,0.707107;3.14159rad)
  Support = -> [Pocket]
FEATURE [PartDesign::CoordinateSystem] LCS_Fasten_4
  AttacherType = Attacher::AttachEngine3D
  MapMode = 11
  Placement = pos=(38,10,-1) rot=(0.707107,0,0.707107;3.14159rad)
  Support = -> [Pocket]
FEATURE [App::Part] CageTop  label="Rail_top"
  Group = -> [LCS_0,Body,Screw_LCS,MountPoint_LCS,LCS_Fasten_1,LCS_Fasten_2,LCS_Fasten_3,LCS_Fasten_4]
  Origin = -> Origin001
